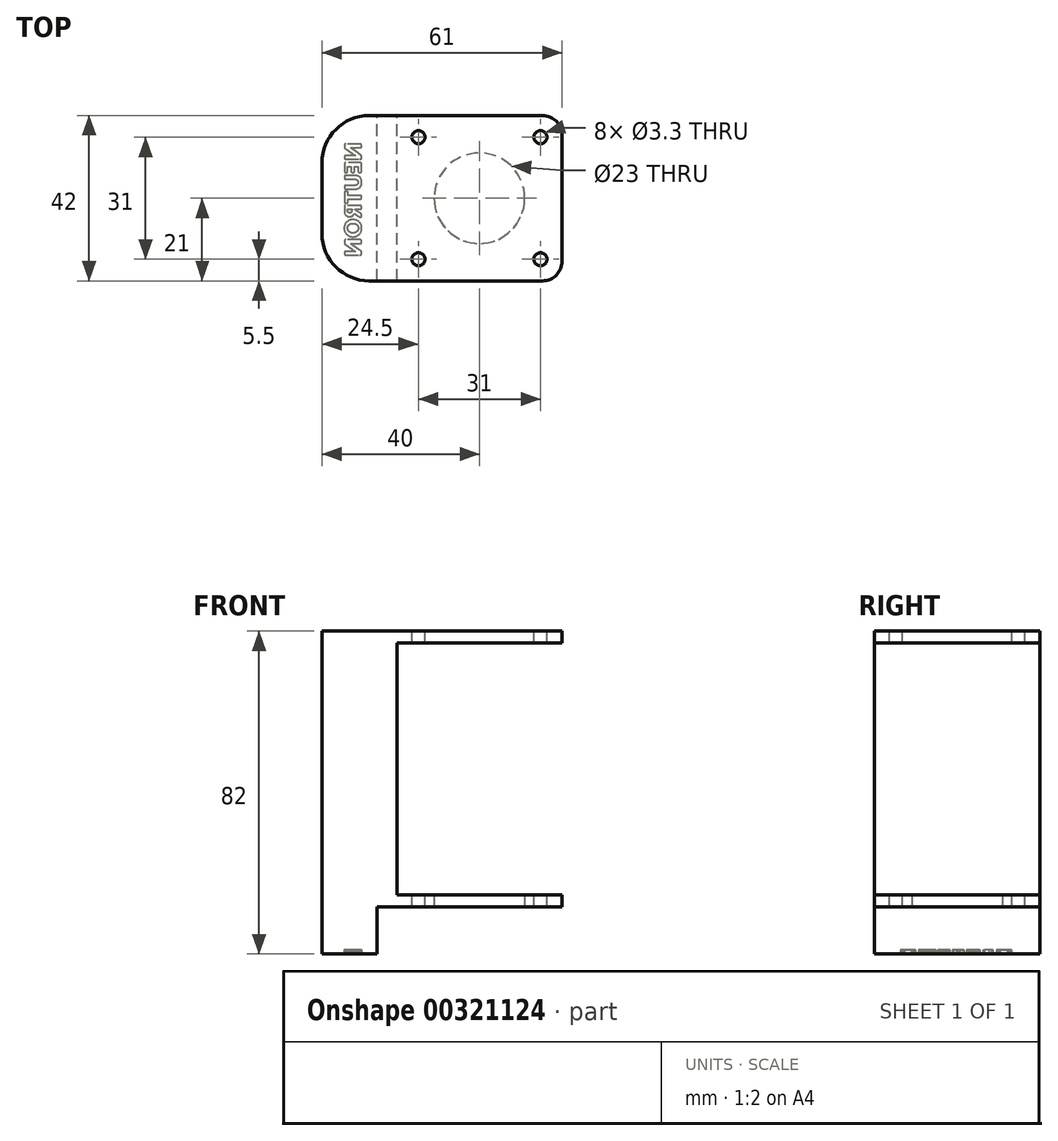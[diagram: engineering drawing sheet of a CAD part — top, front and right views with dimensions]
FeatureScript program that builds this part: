
annotation { "Feature Type Name" : "Feature", "Feature Type Description" : "" }
export const myFeature = defineFeature(function(context is Context, id is Id, definition is map)
    precondition{}
    {
        {
            var Q0;
            Q0=qCreatedBy(makeId("Top.planeOp"),FACE);
            var sketch = newSketch(context, id + "F0", { "sketchPlane" : qUnion([Q0])});
            skLineSegment(sketch, "E0.bottom", {"start": v(21, -21) * mm, "end": v(-21, -21) * mm});
            skLineSegment(sketch, "E0.top", {"start": v(21, 21) * mm, "end": v(-21, 21) * mm});
            skLineSegment(sketch, "E0.left", {"start": v(21, -21) * mm, "end": v(21, 21) * mm});
            skLineSegment(sketch, "E0.right", {"start": v(-21, -21) * mm, "end": v(-21, 21) * mm});
            skPoint(sketch, "E0.middle", {"position": v(0, 0) * mm});
            skSolve(sketch);
        }
        {
            var Q0;
            Q0=makeQuery(id+"F0.imprint","IMPRINT",FACE,{"disambiguationData":[TD([[makeQuery(id+"F0.imprint","IMPRINT",EDGE,{"derivedFrom":sQuery(id+"F0.wireOp",EDGE,"E0.bottom")}),-1.0]])]});
            extrude(context, id + "F1", {"entities" : qUnion([Q0]), "depth" : 3 * mm});
        }
        {
            var Q0;
            Q0=makeQuery(id+"F1.opExtrude","CAP_FACE",FACE,{"disambiguationData":[OSD([sQuery(id+"F0.wireOp",EDGE,"E0.bottom"),sQuery(id+"F0.wireOp",EDGE,"E0.top"),sQuery(id+"F0.wireOp",EDGE,"E0.left"),sQuery(id+"F0.wireOp",EDGE,"E0.right")])],"isStart":true});
            var sketch = newSketch(context, id + "F2", { "sketchPlane" : qUnion([Q0])});
            skLineSegment(sketch, "E1.bottom", {"start": v(-15.5, 15.5) * mm, "end": v(15.5, 15.5) * mm});
            skLineSegment(sketch, "E1.top", {"start": v(-15.5, -15.5) * mm, "end": v(15.5, -15.5) * mm});
            skLineSegment(sketch, "E1.left", {"start": v(-15.5, 15.5) * mm, "end": v(-15.5, -15.5) * mm});
            skLineSegment(sketch, "E1.right", {"start": v(15.5, 15.5) * mm, "end": v(15.5, -15.5) * mm});
            skPoint(sketch, "E1.middle", {"position": v(0, 0) * mm});
            skCircle(sketch, "E2", {"center": v(0, 0) * mm, "radius": 11.5 * mm});
            skSolve(sketch);
        }
        {
            var Q0;
            Q0=makeQuery(id+"F2.imprint","IMPRINT",FACE,{"disambiguationData":[TD([[makeQuery(id+"F2.imprint","IMPRINT",EDGE,{"derivedFrom":sQuery(id+"F2.wireOp",EDGE,"E2")}),1.0]])]});
            extrude(context, id + "F3", {"entities" : qUnion([Q0]), "operationType" : NewBodyOperationType.REMOVE, "oppositeDirection" : true, "depth" : 25 * mm});
        }
        {
            var Q0;
            Q0=makeQuery(id+"F1.opExtrude","SWEPT_FACE",FACE,{"disambiguationData":[OSD([sQuery(id+"F0.wireOp",EDGE,"E0.right")])]});
            var sketch = newSketch(context, id + "F4", { "sketchPlane" : qUnion([Q0])});
            skLineSegment(sketch, "E3.bottom", {"start": v(21, 0) * mm, "end": v(-21, 0) * mm});
            skLineSegment(sketch, "E3.top", {"start": v(21, 70) * mm, "end": v(-21, 70) * mm});
            skLineSegment(sketch, "E3.left", {"start": v(21, 0) * mm, "end": v(21, 70) * mm});
            skLineSegment(sketch, "E3.right", {"start": v(-21, 0) * mm, "end": v(-21, 70) * mm});
            skSolve(sketch);
        }
        {
            var Q0;
            {var subQ0=sQuery(id+"F4.wireOp",EDGE,"E3.bottom");Q0=makeQuery(id+"F4.imprint","IMPRINT",FACE,{"disambiguationData":[TD([[makeQuery(id+"F4.imprint","IMPRINT",EDGE,{"derivedFrom":subQ0}),-1.0]])]});}
            var Q1;
            {var subQ0=sQuery(id+"F4.wireOp",EDGE,"E3.top");Q1=makeQuery(id+"F4.imprint","IMPRINT",FACE,{"disambiguationData":[TD([[makeQuery(id+"F4.imprint","IMPRINT",EDGE,{"derivedFrom":subQ0}),1.0]])]});}
            extrude(context, id + "F5", {"entities" : qUnion([Q0, Q1]), "operationType" : NewBodyOperationType.ADD, "depth" : 19 * mm});
        }
        {
            var Q0;
            Q0=makeQuery(id+"F5.opExtrude","CAP_FACE",FACE,{"disambiguationData":[OSD([sQuery(id+"F4.wireOp",EDGE,"E3.bottom"),sQuery(id+"F4.wireOp",EDGE,"E3.top"),sQuery(id+"F4.wireOp",EDGE,"E3.left"),sQuery(id+"F4.wireOp",EDGE,"E3.right")])],"isStart":true});
            var sketch = newSketch(context, id + "F6", { "sketchPlane" : qUnion([Q0])});
            skLineSegment(sketch, "E4.bottom", {"start": v(21, 70) * mm, "end": v(-21, 70) * mm});
            skLineSegment(sketch, "E4.top", {"start": v(21, 67) * mm, "end": v(-21, 67) * mm});
            skLineSegment(sketch, "E4.left", {"start": v(21, 70) * mm, "end": v(21, 67) * mm});
            skLineSegment(sketch, "E4.right", {"start": v(-21, 70) * mm, "end": v(-21, 67) * mm});
            skSolve(sketch);
        }
        {
            var Q0;
            Q0 = qSketchRegion(id + "F6", true);
            extrude(context, id + "F7", {"entities" : qUnion([Q0]), "operationType" : NewBodyOperationType.ADD, "depth" : 42 * mm});
        }
        {
            var Q0;
            Q0=makeQuery(id+"F1.opExtrude","SWEPT_EDGE",EDGE,{"disambiguationData":[OSD([sQuery(id+"F0.wireOp",EDGE,"E0.top"),sQuery(id+"F0.wireOp",EDGE,"E0.left")])]});
            var Q1;
            Q1=makeQuery(id+"F1.opExtrude","SWEPT_EDGE",EDGE,{"disambiguationData":[OSD([sQuery(id+"F0.wireOp",EDGE,"E0.bottom"),sQuery(id+"F0.wireOp",EDGE,"E0.left")])]});
            var Q2;
            Q2=makeQuery(id+"F7.opExtrude","CAP_EDGE",EDGE,{"disambiguationData":[OSD([sQuery(id+"F6.wireOp",EDGE,"E4.right")])],"isStart":false});
            var Q3;
            Q3=makeQuery(id+"F7.opExtrude","CAP_EDGE",EDGE,{"disambiguationData":[OSD([sQuery(id+"F6.wireOp",EDGE,"E4.left")])],"isStart":false});
            fillet(context, id + "F8", {"entities" : qUnion([Q0, Q1, Q2, Q3]), "radius" : 5 * mm, "tangentPropagation" : true, "allowEdgeOverflow" : false});
        }
        {
            var Q0;
            Q0=sQuery(id+"F2.wireOp",VERTEX,"E1.left.end");
            var Q1;
            Q1=sQuery(id+"F2.wireOp",VERTEX,"E1.right.end");
            var Q2;
            Q2=sQuery(id+"F2.wireOp",VERTEX,"E1.right.start");
            var Q3;
            Q3=sQuery(id+"F2.wireOp",VERTEX,"E1.left.start");
            var Q4;
            Q4=makeQuery(id+"F1.opExtrude","SWEPT_BODY",BODY,{"disambiguationData":[OSD([sQuery(id+"F0.wireOp",EDGE,"E0.bottom"),sQuery(id+"F0.wireOp",EDGE,"E0.top"),sQuery(id+"F0.wireOp",EDGE,"E0.left"),sQuery(id+"F0.wireOp",EDGE,"E0.right")])]});
            hole(context, id + "F9", {"style" : HoleStyle.SIMPLE, "endStyle" : HoleEndStyle.THROUGH, "standardTappedOrClearance" : lookupTablePath({ "standard" : "ISO", "fit" : "Normal", "size" : "M3", "type" : "Clearance" }), "standardBlindInLast" : lookupTablePath({ "fit" : "Standard", "standard" : "ISO", "size" : "M3", "type" : "Clearance" }), "holeDiameter" : 3.3 * mm, "tappedDepth" : 12 * mm, "tapClearance" : 3, "locations" : qUnion([Q0, Q1, Q2, Q3]), "scope" : qUnion([Q4])});
        }
        {
            var Q0;
            Q0=makeQuery(id+"F5.opExtrude","CAP_EDGE",EDGE,{"disambiguationData":[OSD([sQuery(id+"F4.wireOp",EDGE,"E3.left")])],"isStart":false});
            var Q1;
            Q1=makeQuery(id+"F5.opExtrude","CAP_EDGE",EDGE,{"disambiguationData":[OSD([sQuery(id+"F4.wireOp",EDGE,"E3.right")])],"isStart":false});
            fillet(context, id + "F10", {"entities" : qUnion([Q0, Q1]), "radius" : 12 * mm, "tangentPropagation" : true, "allowEdgeOverflow" : false});
        }
        {
            var Q0;
            Q0=makeQuery(id+"F5.boolean.opBoolean","MERGE",FACE,{"derivedFrom":[makeQuery(id+"F1.opExtrude","CAP_FACE",FACE,{"disambiguationData":[OSD([sQuery(id+"F0.wireOp",EDGE,"E0.bottom"),sQuery(id+"F0.wireOp",EDGE,"E0.top"),sQuery(id+"F0.wireOp",EDGE,"E0.left"),sQuery(id+"F0.wireOp",EDGE,"E0.right")])],"isStart":true}),makeQuery(id+"F5.opExtrude","SWEPT_FACE",FACE,{"disambiguationData":[OSD([sQuery(id+"F4.wireOp",EDGE,"E3.bottom")])]})]});
            var sketch = newSketch(context, id + "F11", { "sketchPlane" : qUnion([Q0])});
            skLineSegment(sketch, "E5", {"start": v(-26, 21) * mm, "end": v(-26, -21) * mm});
            skSolve(sketch);
        }
        {
            var Q0;
            Q0 = qSketchRegion(id + "F11", true);
            var Q1;
            Q1=makeQuery(id+"F11.imprint","IMPRINT",FACE,{"disambiguationData":[TD([[makeQuery(id+"F11.imprint","IMPRINT",EDGE,{"derivedFrom":sQuery(id+"F11.wireOp",EDGE,"xwHfM6YB-dKn8-eSAS-4Oin-q8f2QlFwRjm7")}),1.0]])]});
            var Q2;
            {var subQ6=sQuery(id+"F11.wireOp",EDGE,"E5");Q2=makeQuery(id+"F11.imprint","IMPRINT",FACE,{"disambiguationData":[TD([[makeQuery(id+"F11.imprint","IMPRINT",EDGE,{"derivedFrom":subQ6}),-1.0]])]});}
            extrude(context, id + "F12", {"entities" : qUnion([Q0, Q1, Q2]), "operationType" : NewBodyOperationType.ADD, "depth" : 12 * mm});
        }
        {
            var Q0;
            Q0=makeQuery(id+"F12.opExtrude","CAP_FACE",FACE,{"disambiguationData":[OSD([sQuery(id+"F0.wireOp",EDGE,"E0.bottom"),sQuery(id+"F0.wireOp",EDGE,"E0.top"),sQuery(id+"F0.wireOp",EDGE,"E0.left"),sQuery(id+"F0.wireOp",EDGE,"E0.right"),sQuery(id+"F4.wireOp",EDGE,"E3.bottom"),sQuery(id+"F4.wireOp",EDGE,"E3.left"),sQuery(id+"F4.wireOp",EDGE,"E3.right"),sQuery(id+"F11.wireOp",EDGE,"xwHfM6YB-dKn8-eSAS-4Oin-q8f2QlFwRjm7")])],"isStart":false});
            var sketch = newSketch(context, id + "F13", { "sketchPlane" : qUnion([Q0])});
            skLineSegment(sketch, "E6", {"start": v(-34.33, -10.53) * mm, "end": v(-34.33, -10.5) * mm});
            skLineSegment(sketch, "E7", {"start": v(-34.33, -10.5) * mm, "end": v(-34.33, -10.44) * mm});
            skLineSegment(sketch, "E8", {"start": v(-34.33, -10.44) * mm, "end": v(-34.33, -10.36) * mm});
            skLineSegment(sketch, "E9", {"start": v(-34.33, -10.36) * mm, "end": v(-34.33, -10.28) * mm});
            skLineSegment(sketch, "E10", {"start": v(-34.33, -10.28) * mm, "end": v(-34.33, -10.23) * mm});
            skLineSegment(sketch, "E11", {"start": v(-34.33, -10.23) * mm, "end": v(-34.33, -10.18) * mm});
            skLineSegment(sketch, "E12", {"start": v(-34.33, -10.18) * mm, "end": v(-34.3, -10.1) * mm});
            skLineSegment(sketch, "E13", {"start": v(-34.3, -10.1) * mm, "end": v(-34.26, -10.02) * mm});
            skLineSegment(sketch, "E14", {"start": v(-34.26, -10.02) * mm, "end": v(-34.2, -9.97) * mm});
            skLineSegment(sketch, "E15", {"start": v(-34.2, -9.97) * mm, "end": v(-34.12, -9.93) * mm});
            skLineSegment(sketch, "E16", {"start": v(-34.12, -9.93) * mm, "end": v(-34.03, -9.91) * mm});
            skLineSegment(sketch, "E17", {"start": v(-34.03, -9.91) * mm, "end": v(-33.76, -9.91) * mm});
            skLineSegment(sketch, "E18", {"start": v(-33.76, -9.91) * mm, "end": v(-33.01, -9.91) * mm});
            skLineSegment(sketch, "E19", {"start": v(-33.01, -9.91) * mm, "end": v(-32.03, -9.91) * mm});
            skLineSegment(sketch, "E20", {"start": v(-32.03, -9.91) * mm, "end": v(-31.07, -9.91) * mm});
            skLineSegment(sketch, "E21", {"start": v(-31.07, -9.91) * mm, "end": v(-30.41, -9.91) * mm});
            skLineSegment(sketch, "E22", {"start": v(-30.41, -9.91) * mm, "end": v(-30.23, -9.91) * mm});
            skLineSegment(sketch, "E23", {"start": v(-30.23, -9.91) * mm, "end": v(-30.15, -9.93) * mm});
            skLineSegment(sketch, "E24", {"start": v(-30.15, -9.93) * mm, "end": v(-30.07, -9.98) * mm});
            skLineSegment(sketch, "E25", {"start": v(-30.07, -9.98) * mm, "end": v(-30.01, -10.04) * mm});
            skLineSegment(sketch, "E26", {"start": v(-30.01, -10.04) * mm, "end": v(-29.97, -10.11) * mm});
            skLineSegment(sketch, "E27", {"start": v(-29.97, -10.11) * mm, "end": v(-29.95, -10.2) * mm});
            skLineSegment(sketch, "E28", {"start": v(-29.95, -10.2) * mm, "end": v(-29.95, -10.25) * mm});
            skLineSegment(sketch, "E29", {"start": v(-29.95, -10.25) * mm, "end": v(-29.95, -10.33) * mm});
            skLineSegment(sketch, "E30", {"start": v(-29.95, -10.33) * mm, "end": v(-29.95, -10.45) * mm});
            skLineSegment(sketch, "E31", {"start": v(-29.95, -10.45) * mm, "end": v(-29.95, -10.56) * mm});
            skLineSegment(sketch, "E32", {"start": v(-29.95, -10.56) * mm, "end": v(-29.95, -10.65) * mm});
            skLineSegment(sketch, "E33", {"start": v(-29.95, -10.65) * mm, "end": v(-29.95, -10.68) * mm});
            skLineSegment(sketch, "E34", {"start": v(-29.95, -10.68) * mm, "end": v(-29.96, -10.74) * mm});
            skLineSegment(sketch, "E35", {"start": v(-29.96, -10.74) * mm, "end": v(-29.98, -10.79) * mm});
            skLineSegment(sketch, "E36", {"start": v(-29.98, -10.79) * mm, "end": v(-30, -10.83) * mm});
            skLineSegment(sketch, "E37", {"start": v(-30, -10.83) * mm, "end": v(-30.03, -10.88) * mm});
            skLineSegment(sketch, "E38", {"start": v(-30.03, -10.88) * mm, "end": v(-30.07, -10.91) * mm});
            skLineSegment(sketch, "E39", {"start": v(-30.07, -10.91) * mm, "end": v(-30.2, -11) * mm});
            skLineSegment(sketch, "E40", {"start": v(-30.2, -11) * mm, "end": v(-30.67, -11.34) * mm});
            skLineSegment(sketch, "E41", {"start": v(-30.67, -11.34) * mm, "end": v(-31.35, -11.82) * mm});
            skLineSegment(sketch, "E42", {"start": v(-31.35, -11.82) * mm, "end": v(-32.06, -12.32) * mm});
            skLineSegment(sketch, "E43", {"start": v(-32.06, -12.32) * mm, "end": v(-32.6, -12.7) * mm});
            skLineSegment(sketch, "E44", {"start": v(-32.6, -12.7) * mm, "end": v(-32.78, -12.83) * mm});
            skLineSegment(sketch, "E45", {"start": v(-32.78, -12.83) * mm, "end": v(-32.52, -12.83) * mm});
            skLineSegment(sketch, "E46", {"start": v(-32.52, -12.83) * mm, "end": v(-31.97, -12.83) * mm});
            skLineSegment(sketch, "E47", {"start": v(-31.97, -12.83) * mm, "end": v(-31.3, -12.83) * mm});
            skLineSegment(sketch, "E48", {"start": v(-31.3, -12.83) * mm, "end": v(-30.68, -12.83) * mm});
            skLineSegment(sketch, "E49", {"start": v(-30.68, -12.83) * mm, "end": v(-30.3, -12.83) * mm});
            skLineSegment(sketch, "E50", {"start": v(-30.3, -12.83) * mm, "end": v(-30.21, -12.84) * mm});
            skLineSegment(sketch, "E51", {"start": v(-30.21, -12.84) * mm, "end": v(-30.13, -12.86) * mm});
            skLineSegment(sketch, "E52", {"start": v(-30.13, -12.86) * mm, "end": v(-30.06, -12.9) * mm});
            skLineSegment(sketch, "E53", {"start": v(-30.06, -12.9) * mm, "end": v(-30, -12.97) * mm});
            skLineSegment(sketch, "E54", {"start": v(-30, -12.97) * mm, "end": v(-29.97, -13.05) * mm});
            skLineSegment(sketch, "E55", {"start": v(-29.97, -13.05) * mm, "end": v(-29.95, -13.14) * mm});
            skLineSegment(sketch, "E56", {"start": v(-29.95, -13.14) * mm, "end": v(-29.95, -13.17) * mm});
            skLineSegment(sketch, "E57", {"start": v(-29.95, -13.17) * mm, "end": v(-29.95, -13.24) * mm});
            skLineSegment(sketch, "E58", {"start": v(-29.95, -13.24) * mm, "end": v(-29.95, -13.32) * mm});
            skLineSegment(sketch, "E59", {"start": v(-29.95, -13.32) * mm, "end": v(-29.95, -13.4) * mm});
            skLineSegment(sketch, "E60", {"start": v(-29.95, -13.4) * mm, "end": v(-29.95, -13.46) * mm});
            skLineSegment(sketch, "E61", {"start": v(-29.95, -13.46) * mm, "end": v(-29.96, -13.5) * mm});
            skLineSegment(sketch, "E62", {"start": v(-29.96, -13.5) * mm, "end": v(-29.98, -13.6) * mm});
            skLineSegment(sketch, "E63", {"start": v(-29.98, -13.6) * mm, "end": v(-30.02, -13.66) * mm});
            skLineSegment(sketch, "E64", {"start": v(-30.02, -13.66) * mm, "end": v(-30.09, -13.72) * mm});
            skLineSegment(sketch, "E65", {"start": v(-30.09, -13.72) * mm, "end": v(-30.16, -13.76) * mm});
            skLineSegment(sketch, "E66", {"start": v(-30.16, -13.76) * mm, "end": v(-30.25, -13.78) * mm});
            skLineSegment(sketch, "E67", {"start": v(-30.25, -13.78) * mm, "end": v(-30.52, -13.78) * mm});
            skLineSegment(sketch, "E68", {"start": v(-30.52, -13.78) * mm, "end": v(-31.27, -13.78) * mm});
            skLineSegment(sketch, "E69", {"start": v(-31.27, -13.78) * mm, "end": v(-32.25, -13.78) * mm});
            skLineSegment(sketch, "E70", {"start": v(-32.25, -13.78) * mm, "end": v(-33.2, -13.78) * mm});
            skLineSegment(sketch, "E71", {"start": v(-33.2, -13.78) * mm, "end": v(-33.87, -13.78) * mm});
            skLineSegment(sketch, "E72", {"start": v(-33.87, -13.78) * mm, "end": v(-34.05, -13.77) * mm});
            skLineSegment(sketch, "E73", {"start": v(-34.05, -13.77) * mm, "end": v(-34.14, -13.75) * mm});
            skLineSegment(sketch, "E74", {"start": v(-34.14, -13.75) * mm, "end": v(-34.21, -13.71) * mm});
            skLineSegment(sketch, "E75", {"start": v(-34.21, -13.71) * mm, "end": v(-34.27, -13.65) * mm});
            skLineSegment(sketch, "E76", {"start": v(-34.27, -13.65) * mm, "end": v(-34.31, -13.57) * mm});
            skLineSegment(sketch, "E77", {"start": v(-34.31, -13.57) * mm, "end": v(-34.33, -13.49) * mm});
            skLineSegment(sketch, "E78", {"start": v(-34.33, -13.49) * mm, "end": v(-34.33, -13.44) * mm});
            skLineSegment(sketch, "E79", {"start": v(-34.33, -13.44) * mm, "end": v(-34.33, -13.35) * mm});
            skLineSegment(sketch, "E80", {"start": v(-34.33, -13.35) * mm, "end": v(-34.33, -13.23) * mm});
            skLineSegment(sketch, "E81", {"start": v(-34.33, -13.23) * mm, "end": v(-34.33, -13.11) * mm});
            skLineSegment(sketch, "E82", {"start": v(-34.33, -13.11) * mm, "end": v(-34.33, -13.03) * mm});
            skLineSegment(sketch, "E83", {"start": v(-34.33, -13.03) * mm, "end": v(-34.33, -12.99) * mm});
            skLineSegment(sketch, "E84", {"start": v(-34.33, -12.99) * mm, "end": v(-34.32, -12.94) * mm});
            skLineSegment(sketch, "E85", {"start": v(-34.32, -12.94) * mm, "end": v(-34.3, -12.89) * mm});
            skLineSegment(sketch, "E86", {"start": v(-34.3, -12.89) * mm, "end": v(-34.28, -12.84) * mm});
            skLineSegment(sketch, "E87", {"start": v(-34.28, -12.84) * mm, "end": v(-34.25, -12.8) * mm});
            skLineSegment(sketch, "E88", {"start": v(-34.25, -12.8) * mm, "end": v(-34.21, -12.76) * mm});
            skLineSegment(sketch, "E89", {"start": v(-34.21, -12.76) * mm, "end": v(-34.1, -12.67) * mm});
            skLineSegment(sketch, "E90", {"start": v(-34.1, -12.67) * mm, "end": v(-33.62, -12.34) * mm});
            skLineSegment(sketch, "E91", {"start": v(-33.62, -12.34) * mm, "end": v(-32.94, -11.85) * mm});
            skLineSegment(sketch, "E92", {"start": v(-32.94, -11.85) * mm, "end": v(-32.24, -11.35) * mm});
            skLineSegment(sketch, "E93", {"start": v(-32.24, -11.35) * mm, "end": v(-31.7, -10.97) * mm});
            skLineSegment(sketch, "E94", {"start": v(-31.7, -10.97) * mm, "end": v(-31.52, -10.84) * mm});
            skLineSegment(sketch, "E95", {"start": v(-31.52, -10.84) * mm, "end": v(-31.78, -10.84) * mm});
            skLineSegment(sketch, "E96", {"start": v(-31.78, -10.84) * mm, "end": v(-32.33, -10.84) * mm});
            skLineSegment(sketch, "E97", {"start": v(-32.33, -10.84) * mm, "end": v(-33, -10.84) * mm});
            skLineSegment(sketch, "E98", {"start": v(-33, -10.84) * mm, "end": v(-33.6, -10.84) * mm});
            skLineSegment(sketch, "E99", {"start": v(-33.6, -10.84) * mm, "end": v(-33.97, -10.84) * mm});
            skLineSegment(sketch, "E100", {"start": v(-33.97, -10.84) * mm, "end": v(-34.07, -10.83) * mm});
            skLineSegment(sketch, "E101", {"start": v(-34.07, -10.83) * mm, "end": v(-34.15, -10.8) * mm});
            skLineSegment(sketch, "E102", {"start": v(-34.15, -10.8) * mm, "end": v(-34.22, -10.76) * mm});
            skLineSegment(sketch, "E103", {"start": v(-34.22, -10.76) * mm, "end": v(-34.28, -10.7) * mm});
            skLineSegment(sketch, "E104", {"start": v(-34.28, -10.7) * mm, "end": v(-34.32, -10.62) * mm});
            skLineSegment(sketch, "E105", {"start": v(-34.32, -10.62) * mm, "end": v(-34.33, -10.53) * mm});
            skLineSegment(sketch, "E106", {"start": v(-34.33, -8.72) * mm, "end": v(-34.33, -8.52) * mm});
            skLineSegment(sketch, "E107", {"start": v(-34.33, -8.52) * mm, "end": v(-34.33, -8.07) * mm});
            skLineSegment(sketch, "E108", {"start": v(-34.33, -8.07) * mm, "end": v(-34.33, -7.52) * mm});
            skLineSegment(sketch, "E109", {"start": v(-34.33, -7.52) * mm, "end": v(-34.33, -7.06) * mm});
            skLineSegment(sketch, "E110", {"start": v(-34.33, -7.06) * mm, "end": v(-34.33, -6.87) * mm});
            skLineSegment(sketch, "E111", {"start": v(-34.33, -6.87) * mm, "end": v(-34.31, -6.77) * mm});
            skLineSegment(sketch, "E112", {"start": v(-34.31, -6.77) * mm, "end": v(-34.27, -6.69) * mm});
            skLineSegment(sketch, "E113", {"start": v(-34.27, -6.69) * mm, "end": v(-34.2, -6.62) * mm});
            skLineSegment(sketch, "E114", {"start": v(-34.2, -6.62) * mm, "end": v(-34.12, -6.58) * mm});
            skLineSegment(sketch, "E115", {"start": v(-34.12, -6.58) * mm, "end": v(-34.02, -6.56) * mm});
            skLineSegment(sketch, "E116", {"start": v(-34.02, -6.56) * mm, "end": v(-34, -6.56) * mm});
            skLineSegment(sketch, "E117", {"start": v(-34, -6.56) * mm, "end": v(-33.93, -6.56) * mm});
            skLineSegment(sketch, "E118", {"start": v(-33.93, -6.56) * mm, "end": v(-33.86, -6.56) * mm});
            skLineSegment(sketch, "E119", {"start": v(-33.86, -6.56) * mm, "end": v(-33.8, -6.56) * mm});
            skLineSegment(sketch, "E120", {"start": v(-33.8, -6.56) * mm, "end": v(-33.77, -6.56) * mm});
            skLineSegment(sketch, "E121", {"start": v(-33.77, -6.56) * mm, "end": v(-33.67, -6.58) * mm});
            skLineSegment(sketch, "E122", {"start": v(-33.67, -6.58) * mm, "end": v(-33.59, -6.62) * mm});
            skLineSegment(sketch, "E123", {"start": v(-33.59, -6.62) * mm, "end": v(-33.52, -6.69) * mm});
            skLineSegment(sketch, "E124", {"start": v(-33.52, -6.69) * mm, "end": v(-33.48, -6.77) * mm});
            skLineSegment(sketch, "E125", {"start": v(-33.48, -6.77) * mm, "end": v(-33.46, -6.87) * mm});
            skLineSegment(sketch, "E126", {"start": v(-33.46, -6.87) * mm, "end": v(-33.46, -7) * mm});
            skLineSegment(sketch, "E127", {"start": v(-33.46, -7) * mm, "end": v(-33.46, -7.3) * mm});
            skLineSegment(sketch, "E128", {"start": v(-33.46, -7.3) * mm, "end": v(-33.46, -7.66) * mm});
            skLineSegment(sketch, "E129", {"start": v(-33.46, -7.66) * mm, "end": v(-33.46, -7.96) * mm});
            skLineSegment(sketch, "E130", {"start": v(-33.46, -7.96) * mm, "end": v(-33.46, -8.08) * mm});
            skLineSegment(sketch, "E131", {"start": v(-33.46, -8.08) * mm, "end": v(-33.37, -8.08) * mm});
            skLineSegment(sketch, "E132", {"start": v(-33.37, -8.08) * mm, "end": v(-33.15, -8.08) * mm});
            skLineSegment(sketch, "E133", {"start": v(-33.15, -8.08) * mm, "end": v(-32.9, -8.08) * mm});
            skLineSegment(sketch, "E134", {"start": v(-32.9, -8.08) * mm, "end": v(-32.67, -8.08) * mm});
            skLineSegment(sketch, "E135", {"start": v(-32.67, -8.08) * mm, "end": v(-32.58, -8.08) * mm});
            skLineSegment(sketch, "E136", {"start": v(-32.58, -8.08) * mm, "end": v(-32.58, -7.96) * mm});
            skLineSegment(sketch, "E137", {"start": v(-32.58, -7.96) * mm, "end": v(-32.58, -7.66) * mm});
            skLineSegment(sketch, "E138", {"start": v(-32.58, -7.66) * mm, "end": v(-32.58, -7.3) * mm});
            skLineSegment(sketch, "E139", {"start": v(-32.58, -7.3) * mm, "end": v(-32.58, -7) * mm});
            skLineSegment(sketch, "E140", {"start": v(-32.58, -7) * mm, "end": v(-32.58, -6.87) * mm});
            skLineSegment(sketch, "E141", {"start": v(-32.58, -6.87) * mm, "end": v(-32.56, -6.77) * mm});
            skLineSegment(sketch, "E142", {"start": v(-32.56, -6.77) * mm, "end": v(-32.52, -6.69) * mm});
            skLineSegment(sketch, "E143", {"start": v(-32.52, -6.69) * mm, "end": v(-32.45, -6.62) * mm});
            skLineSegment(sketch, "E144", {"start": v(-32.45, -6.62) * mm, "end": v(-32.37, -6.58) * mm});
            skLineSegment(sketch, "E145", {"start": v(-32.37, -6.58) * mm, "end": v(-32.27, -6.56) * mm});
            skLineSegment(sketch, "E146", {"start": v(-32.27, -6.56) * mm, "end": v(-32.25, -6.56) * mm});
            skLineSegment(sketch, "E147", {"start": v(-32.25, -6.56) * mm, "end": v(-32.19, -6.56) * mm});
            skLineSegment(sketch, "E148", {"start": v(-32.19, -6.56) * mm, "end": v(-32.12, -6.56) * mm});
            skLineSegment(sketch, "E149", {"start": v(-32.12, -6.56) * mm, "end": v(-32.06, -6.56) * mm});
            skLineSegment(sketch, "E150", {"start": v(-32.06, -6.56) * mm, "end": v(-32.04, -6.56) * mm});
            skLineSegment(sketch, "E151", {"start": v(-32.04, -6.56) * mm, "end": v(-31.94, -6.58) * mm});
            skLineSegment(sketch, "E152", {"start": v(-31.94, -6.58) * mm, "end": v(-31.85, -6.62) * mm});
            skLineSegment(sketch, "E153", {"start": v(-31.85, -6.62) * mm, "end": v(-31.79, -6.69) * mm});
            skLineSegment(sketch, "E154", {"start": v(-31.79, -6.69) * mm, "end": v(-31.74, -6.77) * mm});
            skLineSegment(sketch, "E155", {"start": v(-31.74, -6.77) * mm, "end": v(-31.73, -6.87) * mm});
            skLineSegment(sketch, "E156", {"start": v(-31.73, -6.87) * mm, "end": v(-31.73, -7) * mm});
            skLineSegment(sketch, "E157", {"start": v(-31.73, -7) * mm, "end": v(-31.73, -7.3) * mm});
            skLineSegment(sketch, "E158", {"start": v(-31.73, -7.3) * mm, "end": v(-31.73, -7.66) * mm});
            skLineSegment(sketch, "E159", {"start": v(-31.73, -7.66) * mm, "end": v(-31.73, -7.96) * mm});
            skLineSegment(sketch, "E160", {"start": v(-31.73, -7.96) * mm, "end": v(-31.73, -8.08) * mm});
            skLineSegment(sketch, "E161", {"start": v(-31.73, -8.08) * mm, "end": v(-31.63, -8.08) * mm});
            skLineSegment(sketch, "E162", {"start": v(-31.63, -8.08) * mm, "end": v(-31.4, -8.08) * mm});
            skLineSegment(sketch, "E163", {"start": v(-31.4, -8.08) * mm, "end": v(-31.14, -8.08) * mm});
            skLineSegment(sketch, "E164", {"start": v(-31.14, -8.08) * mm, "end": v(-30.91, -8.08) * mm});
            skLineSegment(sketch, "E165", {"start": v(-30.91, -8.08) * mm, "end": v(-30.82, -8.08) * mm});
            skLineSegment(sketch, "E166", {"start": v(-30.82, -8.08) * mm, "end": v(-30.82, -7.96) * mm});
            skLineSegment(sketch, "E167", {"start": v(-30.82, -7.96) * mm, "end": v(-30.82, -7.66) * mm});
            skLineSegment(sketch, "E168", {"start": v(-30.82, -7.66) * mm, "end": v(-30.82, -7.3) * mm});
            skLineSegment(sketch, "E169", {"start": v(-30.82, -7.3) * mm, "end": v(-30.82, -7) * mm});
            skLineSegment(sketch, "E170", {"start": v(-30.82, -7) * mm, "end": v(-30.82, -6.87) * mm});
            skLineSegment(sketch, "E171", {"start": v(-30.82, -6.87) * mm, "end": v(-30.8, -6.77) * mm});
            skLineSegment(sketch, "E172", {"start": v(-30.8, -6.77) * mm, "end": v(-30.76, -6.69) * mm});
            skLineSegment(sketch, "E173", {"start": v(-30.76, -6.69) * mm, "end": v(-30.7, -6.62) * mm});
            skLineSegment(sketch, "E174", {"start": v(-30.7, -6.62) * mm, "end": v(-30.6, -6.58) * mm});
            skLineSegment(sketch, "E175", {"start": v(-30.6, -6.58) * mm, "end": v(-30.51, -6.56) * mm});
            skLineSegment(sketch, "E176", {"start": v(-30.51, -6.56) * mm, "end": v(-30.48, -6.56) * mm});
            skLineSegment(sketch, "E177", {"start": v(-30.48, -6.56) * mm, "end": v(-30.42, -6.56) * mm});
            skLineSegment(sketch, "E178", {"start": v(-30.42, -6.56) * mm, "end": v(-30.35, -6.56) * mm});
            skLineSegment(sketch, "E179", {"start": v(-30.35, -6.56) * mm, "end": v(-30.29, -6.56) * mm});
            skLineSegment(sketch, "E180", {"start": v(-30.29, -6.56) * mm, "end": v(-30.26, -6.56) * mm});
            skLineSegment(sketch, "E181", {"start": v(-30.26, -6.56) * mm, "end": v(-30.16, -6.58) * mm});
            skLineSegment(sketch, "E182", {"start": v(-30.16, -6.58) * mm, "end": v(-30.08, -6.62) * mm});
            skLineSegment(sketch, "E183", {"start": v(-30.08, -6.62) * mm, "end": v(-30.01, -6.69) * mm});
            skLineSegment(sketch, "E184", {"start": v(-30.01, -6.69) * mm, "end": v(-29.97, -6.77) * mm});
            skLineSegment(sketch, "E185", {"start": v(-29.97, -6.77) * mm, "end": v(-29.95, -6.87) * mm});
            skLineSegment(sketch, "E186", {"start": v(-29.95, -6.87) * mm, "end": v(-29.95, -7.06) * mm});
            skLineSegment(sketch, "E187", {"start": v(-29.95, -7.06) * mm, "end": v(-29.95, -7.52) * mm});
            skLineSegment(sketch, "E188", {"start": v(-29.95, -7.52) * mm, "end": v(-29.95, -8.07) * mm});
            skLineSegment(sketch, "E189", {"start": v(-29.95, -8.07) * mm, "end": v(-29.95, -8.52) * mm});
            skLineSegment(sketch, "E190", {"start": v(-29.95, -8.52) * mm, "end": v(-29.95, -8.72) * mm});
            skLineSegment(sketch, "E191", {"start": v(-29.95, -8.72) * mm, "end": v(-29.97, -8.81) * mm});
            skLineSegment(sketch, "E192", {"start": v(-29.97, -8.81) * mm, "end": v(-30.01, -8.9) * mm});
            skLineSegment(sketch, "E193", {"start": v(-30.01, -8.9) * mm, "end": v(-30.08, -8.97) * mm});
            skLineSegment(sketch, "E194", {"start": v(-30.08, -8.97) * mm, "end": v(-30.16, -9.01) * mm});
            skLineSegment(sketch, "E195", {"start": v(-30.16, -9.01) * mm, "end": v(-30.26, -9.03) * mm});
            skLineSegment(sketch, "E196", {"start": v(-30.26, -9.03) * mm, "end": v(-30.65, -9.03) * mm});
            skLineSegment(sketch, "E197", {"start": v(-30.65, -9.03) * mm, "end": v(-31.58, -9.03) * mm});
            skLineSegment(sketch, "E198", {"start": v(-31.58, -9.03) * mm, "end": v(-32.7, -9.03) * mm});
            skLineSegment(sketch, "E199", {"start": v(-32.7, -9.03) * mm, "end": v(-33.63, -9.03) * mm});
            skLineSegment(sketch, "E200", {"start": v(-33.63, -9.03) * mm, "end": v(-34.02, -9.03) * mm});
            skLineSegment(sketch, "E201", {"start": v(-34.02, -9.03) * mm, "end": v(-34.12, -9.01) * mm});
            skLineSegment(sketch, "E202", {"start": v(-34.12, -9.01) * mm, "end": v(-34.2, -8.97) * mm});
            skLineSegment(sketch, "E203", {"start": v(-34.2, -8.97) * mm, "end": v(-34.27, -8.9) * mm});
            skLineSegment(sketch, "E204", {"start": v(-34.27, -8.9) * mm, "end": v(-34.31, -8.81) * mm});
            skLineSegment(sketch, "E205", {"start": v(-34.31, -8.81) * mm, "end": v(-34.33, -8.72) * mm});
            skLineSegment(sketch, "E206", {"start": v(-34.33, -5.45) * mm, "end": v(-34.33, -5.42) * mm});
            skLineSegment(sketch, "E207", {"start": v(-34.33, -5.42) * mm, "end": v(-34.33, -5.35) * mm});
            skLineSegment(sketch, "E208", {"start": v(-34.33, -5.35) * mm, "end": v(-34.33, -5.27) * mm});
            skLineSegment(sketch, "E209", {"start": v(-34.33, -5.27) * mm, "end": v(-34.33, -5.19) * mm});
            skLineSegment(sketch, "E210", {"start": v(-34.33, -5.19) * mm, "end": v(-34.33, -5.14) * mm});
            skLineSegment(sketch, "E211", {"start": v(-34.33, -5.14) * mm, "end": v(-34.32, -5.07) * mm});
            skLineSegment(sketch, "E212", {"start": v(-34.32, -5.07) * mm, "end": v(-34.29, -4.99) * mm});
            skLineSegment(sketch, "E213", {"start": v(-34.29, -4.99) * mm, "end": v(-34.23, -4.92) * mm});
            skLineSegment(sketch, "E214", {"start": v(-34.23, -4.92) * mm, "end": v(-34.16, -4.87) * mm});
            skLineSegment(sketch, "E215", {"start": v(-34.16, -4.87) * mm, "end": v(-34.07, -4.84) * mm});
            skLineSegment(sketch, "E216", {"start": v(-34.07, -4.84) * mm, "end": v(-33.97, -4.83) * mm});
            skLineSegment(sketch, "E217", {"start": v(-33.97, -4.83) * mm, "end": v(-33.57, -4.83) * mm});
            skLineSegment(sketch, "E218", {"start": v(-33.57, -4.83) * mm, "end": v(-32.94, -4.83) * mm});
            skLineSegment(sketch, "E219", {"start": v(-32.94, -4.83) * mm, "end": v(-32.29, -4.83) * mm});
            skLineSegment(sketch, "E220", {"start": v(-32.29, -4.83) * mm, "end": v(-31.8, -4.83) * mm});
            skLineSegment(sketch, "E221", {"start": v(-31.8, -4.83) * mm, "end": v(-31.62, -4.83) * mm});
            skLineSegment(sketch, "E222", {"start": v(-31.62, -4.83) * mm, "end": v(-31.49, -4.82) * mm});
            skLineSegment(sketch, "E223", {"start": v(-31.49, -4.82) * mm, "end": v(-31.37, -4.8) * mm});
            skLineSegment(sketch, "E224", {"start": v(-31.37, -4.8) * mm, "end": v(-31.25, -4.76) * mm});
            skLineSegment(sketch, "E225", {"start": v(-31.25, -4.76) * mm, "end": v(-31.15, -4.7) * mm});
            skLineSegment(sketch, "E226", {"start": v(-31.15, -4.7) * mm, "end": v(-31.06, -4.63) * mm});
            skLineSegment(sketch, "E227", {"start": v(-31.06, -4.63) * mm, "end": v(-30.98, -4.55) * mm});
            skLineSegment(sketch, "E228", {"start": v(-30.98, -4.55) * mm, "end": v(-30.92, -4.46) * mm});
            skLineSegment(sketch, "E229", {"start": v(-30.92, -4.46) * mm, "end": v(-30.87, -4.35) * mm});
            skLineSegment(sketch, "E230", {"start": v(-30.87, -4.35) * mm, "end": v(-30.84, -4.24) * mm});
            skLineSegment(sketch, "E231", {"start": v(-30.84, -4.24) * mm, "end": v(-30.83, -4.12) * mm});
            skLineSegment(sketch, "E232", {"start": v(-30.83, -4.12) * mm, "end": v(-30.83, -3.99) * mm});
            skLineSegment(sketch, "E233", {"start": v(-30.83, -3.99) * mm, "end": v(-30.85, -3.85) * mm});
            skLineSegment(sketch, "E234", {"start": v(-30.85, -3.85) * mm, "end": v(-30.89, -3.73) * mm});
            skLineSegment(sketch, "E235", {"start": v(-30.89, -3.73) * mm, "end": v(-30.94, -3.63) * mm});
            skLineSegment(sketch, "E236", {"start": v(-30.94, -3.63) * mm, "end": v(-31, -3.53) * mm});
            skLineSegment(sketch, "E237", {"start": v(-31, -3.53) * mm, "end": v(-31.1, -3.45) * mm});
            skLineSegment(sketch, "E238", {"start": v(-31.1, -3.45) * mm, "end": v(-31.2, -3.38) * mm});
            skLineSegment(sketch, "E239", {"start": v(-31.2, -3.38) * mm, "end": v(-31.3, -3.33) * mm});
            skLineSegment(sketch, "E240", {"start": v(-31.3, -3.33) * mm, "end": v(-31.43, -3.3) * mm});
            skLineSegment(sketch, "E241", {"start": v(-31.43, -3.3) * mm, "end": v(-31.57, -3.28) * mm});
            skLineSegment(sketch, "E242", {"start": v(-31.57, -3.28) * mm, "end": v(-31.7, -3.27) * mm});
            skLineSegment(sketch, "E243", {"start": v(-31.7, -3.27) * mm, "end": v(-31.99, -3.27) * mm});
            skLineSegment(sketch, "E244", {"start": v(-31.99, -3.27) * mm, "end": v(-32.55, -3.27) * mm});
            skLineSegment(sketch, "E245", {"start": v(-32.55, -3.27) * mm, "end": v(-33.2, -3.27) * mm});
            skLineSegment(sketch, "E246", {"start": v(-33.2, -3.27) * mm, "end": v(-33.76, -3.27) * mm});
            skLineSegment(sketch, "E247", {"start": v(-33.76, -3.27) * mm, "end": v(-34.02, -3.27) * mm});
            skLineSegment(sketch, "E248", {"start": v(-34.02, -3.27) * mm, "end": v(-34.1, -3.26) * mm});
            skLineSegment(sketch, "E249", {"start": v(-34.1, -3.26) * mm, "end": v(-34.19, -3.22) * mm});
            skLineSegment(sketch, "E250", {"start": v(-34.19, -3.22) * mm, "end": v(-34.25, -3.16) * mm});
            skLineSegment(sketch, "E251", {"start": v(-34.25, -3.16) * mm, "end": v(-34.3, -3.09) * mm});
            skLineSegment(sketch, "E252", {"start": v(-34.3, -3.09) * mm, "end": v(-34.33, -3) * mm});
            skLineSegment(sketch, "E253", {"start": v(-34.33, -3) * mm, "end": v(-34.33, -2.95) * mm});
            skLineSegment(sketch, "E254", {"start": v(-34.33, -2.95) * mm, "end": v(-34.33, -2.9) * mm});
            skLineSegment(sketch, "E255", {"start": v(-34.33, -2.9) * mm, "end": v(-34.33, -2.8) * mm});
            skLineSegment(sketch, "E256", {"start": v(-34.33, -2.8) * mm, "end": v(-34.33, -2.72) * mm});
            skLineSegment(sketch, "E257", {"start": v(-34.33, -2.72) * mm, "end": v(-34.33, -2.66) * mm});
            skLineSegment(sketch, "E258", {"start": v(-34.33, -2.66) * mm, "end": v(-34.33, -2.62) * mm});
            skLineSegment(sketch, "E259", {"start": v(-34.33, -2.62) * mm, "end": v(-34.3, -2.53) * mm});
            skLineSegment(sketch, "E260", {"start": v(-34.3, -2.53) * mm, "end": v(-34.25, -2.45) * mm});
            skLineSegment(sketch, "E261", {"start": v(-34.25, -2.45) * mm, "end": v(-34.19, -2.4) * mm});
            skLineSegment(sketch, "E262", {"start": v(-34.19, -2.4) * mm, "end": v(-34.1, -2.35) * mm});
            skLineSegment(sketch, "E263", {"start": v(-34.1, -2.35) * mm, "end": v(-34.02, -2.34) * mm});
            skLineSegment(sketch, "E264", {"start": v(-34.02, -2.34) * mm, "end": v(-33.73, -2.34) * mm});
            skLineSegment(sketch, "E265", {"start": v(-33.73, -2.34) * mm, "end": v(-33.13, -2.34) * mm});
            skLineSegment(sketch, "E266", {"start": v(-33.13, -2.34) * mm, "end": v(-32.42, -2.34) * mm});
            skLineSegment(sketch, "E267", {"start": v(-32.42, -2.34) * mm, "end": v(-31.8, -2.34) * mm});
            skLineSegment(sketch, "E268", {"start": v(-31.8, -2.34) * mm, "end": v(-31.5, -2.34) * mm});
            skLineSegment(sketch, "E269", {"start": v(-31.5, -2.34) * mm, "end": v(-31.38, -2.35) * mm});
            skLineSegment(sketch, "E270", {"start": v(-31.38, -2.35) * mm, "end": v(-31.23, -2.37) * mm});
            skLineSegment(sketch, "E271", {"start": v(-31.23, -2.37) * mm, "end": v(-31.08, -2.4) * mm});
            skLineSegment(sketch, "E272", {"start": v(-31.08, -2.4) * mm, "end": v(-30.94, -2.45) * mm});
            skLineSegment(sketch, "E273", {"start": v(-30.94, -2.45) * mm, "end": v(-30.79, -2.5) * mm});
            skLineSegment(sketch, "E274", {"start": v(-30.79, -2.5) * mm, "end": v(-30.64, -2.58) * mm});
            skLineSegment(sketch, "E275", {"start": v(-30.64, -2.58) * mm, "end": v(-30.5, -2.67) * mm});
            skLineSegment(sketch, "E276", {"start": v(-30.5, -2.67) * mm, "end": v(-30.37, -2.78) * mm});
            skLineSegment(sketch, "E277", {"start": v(-30.37, -2.78) * mm, "end": v(-30.26, -2.9) * mm});
            skLineSegment(sketch, "E278", {"start": v(-30.26, -2.9) * mm, "end": v(-30.17, -3.03) * mm});
            skLineSegment(sketch, "E279", {"start": v(-30.17, -3.03) * mm, "end": v(-30.08, -3.18) * mm});
            skLineSegment(sketch, "E280", {"start": v(-30.08, -3.18) * mm, "end": v(-30.01, -3.34) * mm});
            skLineSegment(sketch, "E281", {"start": v(-30.01, -3.34) * mm, "end": v(-29.96, -3.5) * mm});
            skLineSegment(sketch, "E282", {"start": v(-29.96, -3.5) * mm, "end": v(-29.92, -3.68) * mm});
            skLineSegment(sketch, "E283", {"start": v(-29.92, -3.68) * mm, "end": v(-29.9, -3.85) * mm});
            skLineSegment(sketch, "E284", {"start": v(-29.9, -3.85) * mm, "end": v(-29.9, -4.05) * mm});
            skLineSegment(sketch, "E285", {"start": v(-29.9, -4.05) * mm, "end": v(-29.91, -4.37) * mm});
            skLineSegment(sketch, "E286", {"start": v(-29.91, -4.37) * mm, "end": v(-29.97, -4.66) * mm});
            skLineSegment(sketch, "E287", {"start": v(-29.97, -4.66) * mm, "end": v(-30.06, -4.91) * mm});
            skLineSegment(sketch, "E288", {"start": v(-30.06, -4.91) * mm, "end": v(-30.2, -5.13) * mm});
            skLineSegment(sketch, "E289", {"start": v(-30.2, -5.13) * mm, "end": v(-30.36, -5.31) * mm});
            skLineSegment(sketch, "E290", {"start": v(-30.36, -5.31) * mm, "end": v(-30.55, -5.46) * mm});
            skLineSegment(sketch, "E291", {"start": v(-30.55, -5.46) * mm, "end": v(-30.74, -5.58) * mm});
            skLineSegment(sketch, "E292", {"start": v(-30.74, -5.58) * mm, "end": v(-30.94, -5.67) * mm});
            skLineSegment(sketch, "E293", {"start": v(-30.94, -5.67) * mm, "end": v(-31.14, -5.73) * mm});
            skLineSegment(sketch, "E294", {"start": v(-31.14, -5.73) * mm, "end": v(-31.35, -5.76) * mm});
            skLineSegment(sketch, "E295", {"start": v(-31.35, -5.76) * mm, "end": v(-31.52, -5.76) * mm});
            skLineSegment(sketch, "E296", {"start": v(-31.52, -5.76) * mm, "end": v(-31.97, -5.76) * mm});
            skLineSegment(sketch, "E297", {"start": v(-31.97, -5.76) * mm, "end": v(-32.66, -5.76) * mm});
            skLineSegment(sketch, "E298", {"start": v(-32.66, -5.76) * mm, "end": v(-33.37, -5.76) * mm});
            skLineSegment(sketch, "E299", {"start": v(-33.37, -5.76) * mm, "end": v(-33.88, -5.76) * mm});
            skLineSegment(sketch, "E300", {"start": v(-33.88, -5.76) * mm, "end": v(-34.05, -5.76) * mm});
            skLineSegment(sketch, "E301", {"start": v(-34.05, -5.76) * mm, "end": v(-34.14, -5.74) * mm});
            skLineSegment(sketch, "E302", {"start": v(-34.14, -5.74) * mm, "end": v(-34.21, -5.7) * mm});
            skLineSegment(sketch, "E303", {"start": v(-34.21, -5.7) * mm, "end": v(-34.28, -5.63) * mm});
            skLineSegment(sketch, "E304", {"start": v(-34.28, -5.63) * mm, "end": v(-34.31, -5.55) * mm});
            skLineSegment(sketch, "E305", {"start": v(-34.31, -5.55) * mm, "end": v(-34.33, -5.45) * mm});
            skLineSegment(sketch, "E306", {"start": v(-34.33, -1.42) * mm, "end": v(-34.33, -1.3) * mm});
            skLineSegment(sketch, "E307", {"start": v(-34.33, -1.3) * mm, "end": v(-34.33, -0.98) * mm});
            skLineSegment(sketch, "E308", {"start": v(-34.33, -0.98) * mm, "end": v(-34.33, -0.54) * mm});
            skLineSegment(sketch, "E309", {"start": v(-34.33, -0.54) * mm, "end": v(-34.33, -0.05) * mm});
            skLineSegment(sketch, "E310", {"start": v(-34.33, -0.05) * mm, "end": v(-34.33, 0.4) * mm});
            skLineSegment(sketch, "E311", {"start": v(-34.33, 0.4) * mm, "end": v(-34.33, 0.74) * mm});
            skLineSegment(sketch, "E312", {"start": v(-34.33, 0.74) * mm, "end": v(-34.33, 0.9) * mm});
            skLineSegment(sketch, "E313", {"start": v(-34.33, 0.9) * mm, "end": v(-34.32, 0.96) * mm});
            skLineSegment(sketch, "E314", {"start": v(-34.32, 0.96) * mm, "end": v(-34.3, 1.03) * mm});
            skLineSegment(sketch, "E315", {"start": v(-34.3, 1.03) * mm, "end": v(-34.27, 1.09) * mm});
            skLineSegment(sketch, "E316", {"start": v(-34.27, 1.09) * mm, "end": v(-34.22, 1.14) * mm});
            skLineSegment(sketch, "E317", {"start": v(-34.22, 1.14) * mm, "end": v(-34.17, 1.17) * mm});
            skLineSegment(sketch, "E318", {"start": v(-34.17, 1.17) * mm, "end": v(-34.1, 1.2) * mm});
            skLineSegment(sketch, "E319", {"start": v(-34.1, 1.2) * mm, "end": v(-34.04, 1.21) * mm});
            skLineSegment(sketch, "E320", {"start": v(-34.04, 1.21) * mm, "end": v(-34.01, 1.21) * mm});
            skLineSegment(sketch, "E321", {"start": v(-34.01, 1.21) * mm, "end": v(-33.97, 1.21) * mm});
            skLineSegment(sketch, "E322", {"start": v(-33.97, 1.21) * mm, "end": v(-33.92, 1.21) * mm});
            skLineSegment(sketch, "E323", {"start": v(-33.92, 1.21) * mm, "end": v(-33.85, 1.21) * mm});
            skLineSegment(sketch, "E324", {"start": v(-33.85, 1.21) * mm, "end": v(-33.8, 1.21) * mm});
            skLineSegment(sketch, "E325", {"start": v(-33.8, 1.21) * mm, "end": v(-33.74, 1.21) * mm});
            skLineSegment(sketch, "E326", {"start": v(-33.74, 1.21) * mm, "end": v(-33.71, 1.21) * mm});
            skLineSegment(sketch, "E327", {"start": v(-33.71, 1.21) * mm, "end": v(-33.67, 1.21) * mm});
            skLineSegment(sketch, "E328", {"start": v(-33.67, 1.21) * mm, "end": v(-33.6, 1.2) * mm});
            skLineSegment(sketch, "E329", {"start": v(-33.6, 1.2) * mm, "end": v(-33.54, 1.16) * mm});
            skLineSegment(sketch, "E330", {"start": v(-33.54, 1.16) * mm, "end": v(-33.49, 1.12) * mm});
            skLineSegment(sketch, "E331", {"start": v(-33.49, 1.12) * mm, "end": v(-33.45, 1.07) * mm});
            skLineSegment(sketch, "E332", {"start": v(-33.45, 1.07) * mm, "end": v(-33.42, 1.01) * mm});
            skLineSegment(sketch, "E333", {"start": v(-33.42, 1.01) * mm, "end": v(-33.4, 0.94) * mm});
            skLineSegment(sketch, "E334", {"start": v(-33.4, 0.94) * mm, "end": v(-33.4, 0.9) * mm});
            skLineSegment(sketch, "E335", {"start": v(-33.4, 0.9) * mm, "end": v(-33.4, 0.83) * mm});
            skLineSegment(sketch, "E336", {"start": v(-33.4, 0.83) * mm, "end": v(-33.4, 0.72) * mm});
            skLineSegment(sketch, "E337", {"start": v(-33.4, 0.72) * mm, "end": v(-33.4, 0.58) * mm});
            skLineSegment(sketch, "E338", {"start": v(-33.4, 0.58) * mm, "end": v(-33.4, 0.43) * mm});
            skLineSegment(sketch, "E339", {"start": v(-33.4, 0.43) * mm, "end": v(-33.4, 0.31) * mm});
            skLineSegment(sketch, "E340", {"start": v(-33.4, 0.31) * mm, "end": v(-33.4, 0.23) * mm});
            skLineSegment(sketch, "E341", {"start": v(-33.4, 0.23) * mm, "end": v(-33.38, 0.2) * mm});
            skLineSegment(sketch, "E342", {"start": v(-33.38, 0.2) * mm, "end": v(-33.13, 0.2) * mm});
            skLineSegment(sketch, "E343", {"start": v(-33.13, 0.2) * mm, "end": v(-32.64, 0.2) * mm});
            skLineSegment(sketch, "E344", {"start": v(-32.64, 0.2) * mm, "end": v(-32.02, 0.2) * mm});
            skLineSegment(sketch, "E345", {"start": v(-32.02, 0.2) * mm, "end": v(-31.37, 0.2) * mm});
            skLineSegment(sketch, "E346", {"start": v(-31.37, 0.2) * mm, "end": v(-30.79, 0.2) * mm});
            skLineSegment(sketch, "E347", {"start": v(-30.79, 0.2) * mm, "end": v(-30.39, 0.2) * mm});
            skLineSegment(sketch, "E348", {"start": v(-30.39, 0.2) * mm, "end": v(-30.25, 0.2) * mm});
            skLineSegment(sketch, "E349", {"start": v(-30.25, 0.2) * mm, "end": v(-30.18, 0.2) * mm});
            skLineSegment(sketch, "E350", {"start": v(-30.18, 0.2) * mm, "end": v(-30.12, 0.18) * mm});
            skLineSegment(sketch, "E351", {"start": v(-30.12, 0.18) * mm, "end": v(-30.06, 0.14) * mm});
            skLineSegment(sketch, "E352", {"start": v(-30.06, 0.14) * mm, "end": v(-30.02, 0.1) * mm});
            skLineSegment(sketch, "E353", {"start": v(-30.02, 0.1) * mm, "end": v(-29.98, 0.03) * mm});
            skLineSegment(sketch, "E354", {"start": v(-29.98, 0.03) * mm, "end": v(-29.96, -0.03) * mm});
            skLineSegment(sketch, "E355", {"start": v(-29.96, -0.03) * mm, "end": v(-29.95, -0.1) * mm});
            skLineSegment(sketch, "E356", {"start": v(-29.95, -0.1) * mm, "end": v(-29.95, -0.16) * mm});
            skLineSegment(sketch, "E357", {"start": v(-29.95, -0.16) * mm, "end": v(-29.95, -0.22) * mm});
            skLineSegment(sketch, "E358", {"start": v(-29.95, -0.22) * mm, "end": v(-29.95, -0.3) * mm});
            skLineSegment(sketch, "E359", {"start": v(-29.95, -0.3) * mm, "end": v(-29.95, -0.35) * mm});
            skLineSegment(sketch, "E360", {"start": v(-29.95, -0.35) * mm, "end": v(-29.95, -0.4) * mm});
            skLineSegment(sketch, "E361", {"start": v(-29.95, -0.4) * mm, "end": v(-29.95, -0.42) * mm});
            skLineSegment(sketch, "E362", {"start": v(-29.95, -0.42) * mm, "end": v(-29.96, -0.48) * mm});
            skLineSegment(sketch, "E363", {"start": v(-29.96, -0.48) * mm, "end": v(-29.98, -0.55) * mm});
            skLineSegment(sketch, "E364", {"start": v(-29.98, -0.55) * mm, "end": v(-30.01, -0.6) * mm});
            skLineSegment(sketch, "E365", {"start": v(-30.01, -0.6) * mm, "end": v(-30.06, -0.66) * mm});
            skLineSegment(sketch, "E366", {"start": v(-30.06, -0.66) * mm, "end": v(-30.11, -0.7) * mm});
            skLineSegment(sketch, "E367", {"start": v(-30.11, -0.7) * mm, "end": v(-30.17, -0.72) * mm});
            skLineSegment(sketch, "E368", {"start": v(-30.17, -0.72) * mm, "end": v(-30.24, -0.73) * mm});
            skLineSegment(sketch, "E369", {"start": v(-30.24, -0.73) * mm, "end": v(-30.35, -0.73) * mm});
            skLineSegment(sketch, "E370", {"start": v(-30.35, -0.73) * mm, "end": v(-30.72, -0.73) * mm});
            skLineSegment(sketch, "E371", {"start": v(-30.72, -0.73) * mm, "end": v(-31.28, -0.73) * mm});
            skLineSegment(sketch, "E372", {"start": v(-31.28, -0.73) * mm, "end": v(-31.92, -0.73) * mm});
            skLineSegment(sketch, "E373", {"start": v(-31.92, -0.73) * mm, "end": v(-32.56, -0.73) * mm});
            skLineSegment(sketch, "E374", {"start": v(-32.56, -0.73) * mm, "end": v(-33.07, -0.73) * mm});
            skLineSegment(sketch, "E375", {"start": v(-33.07, -0.73) * mm, "end": v(-33.37, -0.73) * mm});
            skLineSegment(sketch, "E376", {"start": v(-33.37, -0.73) * mm, "end": v(-33.4, -0.75) * mm});
            skLineSegment(sketch, "E377", {"start": v(-33.4, -0.75) * mm, "end": v(-33.4, -0.82) * mm});
            skLineSegment(sketch, "E378", {"start": v(-33.4, -0.82) * mm, "end": v(-33.4, -0.94) * mm});
            skLineSegment(sketch, "E379", {"start": v(-33.4, -0.94) * mm, "end": v(-33.4, -1.08) * mm});
            skLineSegment(sketch, "E380", {"start": v(-33.4, -1.08) * mm, "end": v(-33.4, -1.22) * mm});
            skLineSegment(sketch, "E381", {"start": v(-33.4, -1.22) * mm, "end": v(-33.4, -1.34) * mm});
            skLineSegment(sketch, "E382", {"start": v(-33.4, -1.34) * mm, "end": v(-33.4, -1.4) * mm});
            skLineSegment(sketch, "E383", {"start": v(-33.4, -1.4) * mm, "end": v(-33.4, -1.45) * mm});
            skLineSegment(sketch, "E384", {"start": v(-33.4, -1.45) * mm, "end": v(-33.42, -1.52) * mm});
            skLineSegment(sketch, "E385", {"start": v(-33.42, -1.52) * mm, "end": v(-33.44, -1.58) * mm});
            skLineSegment(sketch, "E386", {"start": v(-33.44, -1.58) * mm, "end": v(-33.48, -1.63) * mm});
            skLineSegment(sketch, "E387", {"start": v(-33.48, -1.63) * mm, "end": v(-33.53, -1.68) * mm});
            skLineSegment(sketch, "E388", {"start": v(-33.53, -1.68) * mm, "end": v(-33.6, -1.7) * mm});
            skLineSegment(sketch, "E389", {"start": v(-33.6, -1.7) * mm, "end": v(-33.66, -1.73) * mm});
            skLineSegment(sketch, "E390", {"start": v(-33.66, -1.73) * mm, "end": v(-33.7, -1.73) * mm});
            skLineSegment(sketch, "E391", {"start": v(-33.7, -1.73) * mm, "end": v(-33.74, -1.73) * mm});
            skLineSegment(sketch, "E392", {"start": v(-33.74, -1.73) * mm, "end": v(-33.78, -1.73) * mm});
            skLineSegment(sketch, "E393", {"start": v(-33.78, -1.73) * mm, "end": v(-33.85, -1.73) * mm});
            skLineSegment(sketch, "E394", {"start": v(-33.85, -1.73) * mm, "end": v(-33.91, -1.73) * mm});
            skLineSegment(sketch, "E395", {"start": v(-33.91, -1.73) * mm, "end": v(-33.97, -1.73) * mm});
            skLineSegment(sketch, "E396", {"start": v(-33.97, -1.73) * mm, "end": v(-34, -1.73) * mm});
            skLineSegment(sketch, "E397", {"start": v(-34, -1.73) * mm, "end": v(-34.03, -1.73) * mm});
            skLineSegment(sketch, "E398", {"start": v(-34.03, -1.73) * mm, "end": v(-34.1, -1.72) * mm});
            skLineSegment(sketch, "E399", {"start": v(-34.1, -1.72) * mm, "end": v(-34.16, -1.7) * mm});
            skLineSegment(sketch, "E400", {"start": v(-34.16, -1.7) * mm, "end": v(-34.22, -1.66) * mm});
            skLineSegment(sketch, "E401", {"start": v(-34.22, -1.66) * mm, "end": v(-34.26, -1.61) * mm});
            skLineSegment(sketch, "E402", {"start": v(-34.26, -1.61) * mm, "end": v(-34.3, -1.55) * mm});
            skLineSegment(sketch, "E403", {"start": v(-34.3, -1.55) * mm, "end": v(-34.32, -1.5) * mm});
            skLineSegment(sketch, "E404", {"start": v(-34.32, -1.5) * mm, "end": v(-34.33, -1.42) * mm});
            skLineSegment(sketch, "E405", {"start": v(-34.02, 1.83) * mm, "end": v(-34.1, 1.84) * mm});
            skLineSegment(sketch, "E406", {"start": v(-34.1, 1.84) * mm, "end": v(-34.18, 1.87) * mm});
            skLineSegment(sketch, "E407", {"start": v(-34.18, 1.87) * mm, "end": v(-34.24, 1.92) * mm});
            skLineSegment(sketch, "E408", {"start": v(-34.24, 1.92) * mm, "end": v(-34.3, 1.99) * mm});
            skLineSegment(sketch, "E409", {"start": v(-34.3, 1.99) * mm, "end": v(-34.32, 2.06) * mm});
            skLineSegment(sketch, "E410", {"start": v(-34.32, 2.06) * mm, "end": v(-34.33, 2.14) * mm});
            skLineSegment(sketch, "E411", {"start": v(-34.33, 2.14) * mm, "end": v(-34.33, 2.25) * mm});
            skLineSegment(sketch, "E412", {"start": v(-34.33, 2.25) * mm, "end": v(-34.33, 2.47) * mm});
            skLineSegment(sketch, "E413", {"start": v(-34.33, 2.47) * mm, "end": v(-34.33, 2.76) * mm});
            skLineSegment(sketch, "E414", {"start": v(-34.33, 2.76) * mm, "end": v(-34.33, 3.03) * mm});
            skLineSegment(sketch, "E415", {"start": v(-34.33, 3.03) * mm, "end": v(-34.33, 3.22) * mm});
            skLineSegment(sketch, "E416", {"start": v(-34.33, 3.22) * mm, "end": v(-34.33, 3.32) * mm});
            skLineSegment(sketch, "E417", {"start": v(-34.33, 3.32) * mm, "end": v(-34.31, 3.54) * mm});
            skLineSegment(sketch, "E418", {"start": v(-34.31, 3.54) * mm, "end": v(-34.28, 3.73) * mm});
            skLineSegment(sketch, "E419", {"start": v(-34.28, 3.73) * mm, "end": v(-34.22, 3.91) * mm});
            skLineSegment(sketch, "E420", {"start": v(-34.22, 3.91) * mm, "end": v(-34.15, 4.08) * mm});
            skLineSegment(sketch, "E421", {"start": v(-34.15, 4.08) * mm, "end": v(-34.05, 4.22) * mm});
            skLineSegment(sketch, "E422", {"start": v(-34.05, 4.22) * mm, "end": v(-33.94, 4.36) * mm});
            skLineSegment(sketch, "E423", {"start": v(-33.94, 4.36) * mm, "end": v(-33.81, 4.47) * mm});
            skLineSegment(sketch, "E424", {"start": v(-33.81, 4.47) * mm, "end": v(-33.67, 4.56) * mm});
            skLineSegment(sketch, "E425", {"start": v(-33.67, 4.56) * mm, "end": v(-33.5, 4.62) * mm});
            skLineSegment(sketch, "E426", {"start": v(-33.5, 4.62) * mm, "end": v(-33.34, 4.67) * mm});
            skLineSegment(sketch, "E427", {"start": v(-33.34, 4.67) * mm, "end": v(-33.15, 4.69) * mm});
            skLineSegment(sketch, "E428", {"start": v(-33.15, 4.69) * mm, "end": v(-33, 4.7) * mm});
            skLineSegment(sketch, "E429", {"start": v(-33, 4.7) * mm, "end": v(-32.88, 4.68) * mm});
            skLineSegment(sketch, "E430", {"start": v(-32.88, 4.68) * mm, "end": v(-32.76, 4.66) * mm});
            skLineSegment(sketch, "E431", {"start": v(-32.76, 4.66) * mm, "end": v(-32.64, 4.63) * mm});
            skLineSegment(sketch, "E432", {"start": v(-32.64, 4.63) * mm, "end": v(-32.52, 4.6) * mm});
            skLineSegment(sketch, "E433", {"start": v(-32.52, 4.6) * mm, "end": v(-32.4, 4.54) * mm});
            skLineSegment(sketch, "E434", {"start": v(-32.4, 4.54) * mm, "end": v(-32.28, 4.48) * mm});
            skLineSegment(sketch, "E435", {"start": v(-32.28, 4.48) * mm, "end": v(-32.16, 4.4) * mm});
            skLineSegment(sketch, "E436", {"start": v(-32.16, 4.4) * mm, "end": v(-32.06, 4.3) * mm});
            skLineSegment(sketch, "E437", {"start": v(-32.06, 4.3) * mm, "end": v(-31.96, 4.2) * mm});
            skLineSegment(sketch, "E438", {"start": v(-31.96, 4.2) * mm, "end": v(-31.88, 4.06) * mm});
            skLineSegment(sketch, "E439", {"start": v(-31.88, 4.06) * mm, "end": v(-31.8, 3.92) * mm});
            skLineSegment(sketch, "E440", {"start": v(-31.8, 3.92) * mm, "end": v(-31.72, 3.9) * mm});
            skLineSegment(sketch, "E441", {"start": v(-31.72, 3.9) * mm, "end": v(-31.5, 4.05) * mm});
            skLineSegment(sketch, "E442", {"start": v(-31.5, 4.05) * mm, "end": v(-31.19, 4.27) * mm});
            skLineSegment(sketch, "E443", {"start": v(-31.19, 4.27) * mm, "end": v(-30.85, 4.5) * mm});
            skLineSegment(sketch, "E444", {"start": v(-30.85, 4.5) * mm, "end": v(-30.57, 4.68) * mm});
            skLineSegment(sketch, "E445", {"start": v(-30.57, 4.68) * mm, "end": v(-30.44, 4.77) * mm});
            skLineSegment(sketch, "E446", {"start": v(-30.44, 4.77) * mm, "end": v(-30.35, 4.81) * mm});
            skLineSegment(sketch, "E447", {"start": v(-30.35, 4.81) * mm, "end": v(-30.23, 4.82) * mm});
            skLineSegment(sketch, "E448", {"start": v(-30.23, 4.82) * mm, "end": v(-30.13, 4.8) * mm});
            skLineSegment(sketch, "E449", {"start": v(-30.13, 4.8) * mm, "end": v(-30.04, 4.73) * mm});
            skLineSegment(sketch, "E450", {"start": v(-30.04, 4.73) * mm, "end": v(-29.98, 4.64) * mm});
            skLineSegment(sketch, "E451", {"start": v(-29.98, 4.64) * mm, "end": v(-29.95, 4.52) * mm});
            skLineSegment(sketch, "E452", {"start": v(-29.95, 4.52) * mm, "end": v(-29.95, 4.5) * mm});
            skLineSegment(sketch, "E453", {"start": v(-29.95, 4.5) * mm, "end": v(-29.95, 4.43) * mm});
            skLineSegment(sketch, "E454", {"start": v(-29.95, 4.43) * mm, "end": v(-29.95, 4.35) * mm});
            skLineSegment(sketch, "E455", {"start": v(-29.95, 4.35) * mm, "end": v(-29.95, 4.26) * mm});
            skLineSegment(sketch, "E456", {"start": v(-29.95, 4.26) * mm, "end": v(-29.95, 4.2) * mm});
            skLineSegment(sketch, "E457", {"start": v(-29.95, 4.2) * mm, "end": v(-29.95, 4.17) * mm});
            skLineSegment(sketch, "E458", {"start": v(-29.95, 4.17) * mm, "end": v(-29.96, 4.12) * mm});
            skLineSegment(sketch, "E459", {"start": v(-29.96, 4.12) * mm, "end": v(-29.97, 4.07) * mm});
            skLineSegment(sketch, "E460", {"start": v(-29.97, 4.07) * mm, "end": v(-30, 4.03) * mm});
            skLineSegment(sketch, "E461", {"start": v(-30, 4.03) * mm, "end": v(-30.02, 3.98) * mm});
            skLineSegment(sketch, "E462", {"start": v(-30.02, 3.98) * mm, "end": v(-30.06, 3.95) * mm});
            skLineSegment(sketch, "E463", {"start": v(-30.06, 3.95) * mm, "end": v(-30.1, 3.92) * mm});
            skLineSegment(sketch, "E464", {"start": v(-30.1, 3.92) * mm, "end": v(-30.25, 3.81) * mm});
            skLineSegment(sketch, "E465", {"start": v(-30.25, 3.81) * mm, "end": v(-30.57, 3.6) * mm});
            skLineSegment(sketch, "E466", {"start": v(-30.57, 3.6) * mm, "end": v(-30.96, 3.34) * mm});
            skLineSegment(sketch, "E467", {"start": v(-30.96, 3.34) * mm, "end": v(-31.33, 3.1) * mm});
            skLineSegment(sketch, "E468", {"start": v(-31.33, 3.1) * mm, "end": v(-31.58, 2.92) * mm});
            skLineSegment(sketch, "E469", {"start": v(-31.58, 2.92) * mm, "end": v(-31.65, 2.88) * mm});
            skLineSegment(sketch, "E470", {"start": v(-31.65, 2.88) * mm, "end": v(-31.65, 2.84) * mm});
            skLineSegment(sketch, "E471", {"start": v(-31.65, 2.84) * mm, "end": v(-31.65, 2.82) * mm});
            skLineSegment(sketch, "E472", {"start": v(-31.65, 2.82) * mm, "end": v(-31.65, 2.8) * mm});
            skLineSegment(sketch, "E473", {"start": v(-31.65, 2.8) * mm, "end": v(-31.63, 2.77) * mm});
            skLineSegment(sketch, "E474", {"start": v(-31.63, 2.77) * mm, "end": v(-31.45, 2.77) * mm});
            skLineSegment(sketch, "E475", {"start": v(-31.45, 2.77) * mm, "end": v(-31.14, 2.77) * mm});
            skLineSegment(sketch, "E476", {"start": v(-31.14, 2.77) * mm, "end": v(-30.79, 2.77) * mm});
            skLineSegment(sketch, "E477", {"start": v(-30.79, 2.77) * mm, "end": v(-30.48, 2.77) * mm});
            skLineSegment(sketch, "E478", {"start": v(-30.48, 2.77) * mm, "end": v(-30.29, 2.77) * mm});
            skLineSegment(sketch, "E479", {"start": v(-30.29, 2.77) * mm, "end": v(-30.22, 2.77) * mm});
            skLineSegment(sketch, "E480", {"start": v(-30.22, 2.77) * mm, "end": v(-30.14, 2.75) * mm});
            skLineSegment(sketch, "E481", {"start": v(-30.14, 2.75) * mm, "end": v(-30.07, 2.7) * mm});
            skLineSegment(sketch, "E482", {"start": v(-30.07, 2.7) * mm, "end": v(-30.01, 2.65) * mm});
            skLineSegment(sketch, "E483", {"start": v(-30.01, 2.65) * mm, "end": v(-29.97, 2.58) * mm});
            skLineSegment(sketch, "E484", {"start": v(-29.97, 2.58) * mm, "end": v(-29.95, 2.5) * mm});
            skLineSegment(sketch, "E485", {"start": v(-29.95, 2.5) * mm, "end": v(-29.95, 2.45) * mm});
            skLineSegment(sketch, "E486", {"start": v(-29.95, 2.45) * mm, "end": v(-29.95, 2.4) * mm});
            skLineSegment(sketch, "E487", {"start": v(-29.95, 2.4) * mm, "end": v(-29.95, 2.33) * mm});
            skLineSegment(sketch, "E488", {"start": v(-29.95, 2.33) * mm, "end": v(-29.95, 2.24) * mm});
            skLineSegment(sketch, "E489", {"start": v(-29.95, 2.24) * mm, "end": v(-29.95, 2.18) * mm});
            skLineSegment(sketch, "E490", {"start": v(-29.95, 2.18) * mm, "end": v(-29.95, 2.14) * mm});
            skLineSegment(sketch, "E491", {"start": v(-29.95, 2.14) * mm, "end": v(-29.96, 2.07) * mm});
            skLineSegment(sketch, "E492", {"start": v(-29.96, 2.07) * mm, "end": v(-29.99, 2) * mm});
            skLineSegment(sketch, "E493", {"start": v(-29.99, 2) * mm, "end": v(-30.03, 1.93) * mm});
            skLineSegment(sketch, "E494", {"start": v(-30.03, 1.93) * mm, "end": v(-30.1, 1.88) * mm});
            skLineSegment(sketch, "E495", {"start": v(-30.1, 1.88) * mm, "end": v(-30.17, 1.84) * mm});
            skLineSegment(sketch, "E496", {"start": v(-30.17, 1.84) * mm, "end": v(-30.25, 1.83) * mm});
            skLineSegment(sketch, "E497", {"start": v(-30.25, 1.83) * mm, "end": v(-30.5, 1.83) * mm});
            skLineSegment(sketch, "E498", {"start": v(-30.5, 1.83) * mm, "end": v(-31.17, 1.83) * mm});
            skLineSegment(sketch, "E499", {"start": v(-31.17, 1.83) * mm, "end": v(-32.08, 1.83) * mm});
            skLineSegment(sketch, "E500", {"start": v(-32.08, 1.83) * mm, "end": v(-33.01, 1.83) * mm});
            skLineSegment(sketch, "E501", {"start": v(-33.01, 1.83) * mm, "end": v(-33.73, 1.83) * mm});
            skLineSegment(sketch, "E502", {"start": v(-33.73, 1.83) * mm, "end": v(-34.02, 1.83) * mm});
            skLineSegment(sketch, "E503", {"start": v(-33.55, 2.78) * mm, "end": v(-33.5, 2.78) * mm});
            skLineSegment(sketch, "E504", {"start": v(-33.5, 2.78) * mm, "end": v(-33.38, 2.78) * mm});
            skLineSegment(sketch, "E505", {"start": v(-33.38, 2.78) * mm, "end": v(-33.2, 2.78) * mm});
            skLineSegment(sketch, "E506", {"start": v(-33.2, 2.78) * mm, "end": v(-33, 2.78) * mm});
            skLineSegment(sketch, "E507", {"start": v(-33, 2.78) * mm, "end": v(-32.8, 2.78) * mm});
            skLineSegment(sketch, "E508", {"start": v(-32.8, 2.78) * mm, "end": v(-32.6, 2.78) * mm});
            skLineSegment(sketch, "E509", {"start": v(-32.6, 2.78) * mm, "end": v(-32.47, 2.78) * mm});
            skLineSegment(sketch, "E510", {"start": v(-32.47, 2.78) * mm, "end": v(-32.41, 2.78) * mm});
            skLineSegment(sketch, "E511", {"start": v(-32.41, 2.78) * mm, "end": v(-32.4, 2.8) * mm});
            skLineSegment(sketch, "E512", {"start": v(-32.4, 2.8) * mm, "end": v(-32.4, 2.84) * mm});
            skLineSegment(sketch, "E513", {"start": v(-32.4, 2.84) * mm, "end": v(-32.4, 2.87) * mm});
            skLineSegment(sketch, "E514", {"start": v(-32.4, 2.87) * mm, "end": v(-32.4, 2.9) * mm});
            skLineSegment(sketch, "E515", {"start": v(-32.4, 2.9) * mm, "end": v(-32.4, 2.94) * mm});
            skLineSegment(sketch, "E516", {"start": v(-32.4, 2.94) * mm, "end": v(-32.4, 2.97) * mm});
            skLineSegment(sketch, "E517", {"start": v(-32.4, 2.97) * mm, "end": v(-32.41, 3.1) * mm});
            skLineSegment(sketch, "E518", {"start": v(-32.41, 3.1) * mm, "end": v(-32.43, 3.25) * mm});
            skLineSegment(sketch, "E519", {"start": v(-32.43, 3.25) * mm, "end": v(-32.47, 3.39) * mm});
            skLineSegment(sketch, "E520", {"start": v(-32.47, 3.39) * mm, "end": v(-32.53, 3.5) * mm});
            skLineSegment(sketch, "E521", {"start": v(-32.53, 3.5) * mm, "end": v(-32.6, 3.59) * mm});
            skLineSegment(sketch, "E522", {"start": v(-32.6, 3.59) * mm, "end": v(-32.7, 3.65) * mm});
            skLineSegment(sketch, "E523", {"start": v(-32.7, 3.65) * mm, "end": v(-32.81, 3.7) * mm});
            skLineSegment(sketch, "E524", {"start": v(-32.81, 3.7) * mm, "end": v(-32.94, 3.72) * mm});
            skLineSegment(sketch, "E525", {"start": v(-32.94, 3.72) * mm, "end": v(-33.04, 3.72) * mm});
            skLineSegment(sketch, "E526", {"start": v(-33.04, 3.72) * mm, "end": v(-33.1, 3.72) * mm});
            skLineSegment(sketch, "E527", {"start": v(-33.1, 3.72) * mm, "end": v(-33.15, 3.7) * mm});
            skLineSegment(sketch, "E528", {"start": v(-33.15, 3.7) * mm, "end": v(-33.2, 3.69) * mm});
            skLineSegment(sketch, "E529", {"start": v(-33.2, 3.69) * mm, "end": v(-33.25, 3.66) * mm});
            skLineSegment(sketch, "E530", {"start": v(-33.25, 3.66) * mm, "end": v(-33.3, 3.64) * mm});
            skLineSegment(sketch, "E531", {"start": v(-33.3, 3.64) * mm, "end": v(-33.34, 3.6) * mm});
            skLineSegment(sketch, "E532", {"start": v(-33.34, 3.6) * mm, "end": v(-33.38, 3.56) * mm});
            skLineSegment(sketch, "E533", {"start": v(-33.38, 3.56) * mm, "end": v(-33.42, 3.51) * mm});
            skLineSegment(sketch, "E534", {"start": v(-33.42, 3.51) * mm, "end": v(-33.45, 3.46) * mm});
            skLineSegment(sketch, "E535", {"start": v(-33.45, 3.46) * mm, "end": v(-33.48, 3.4) * mm});
            skLineSegment(sketch, "E536", {"start": v(-33.48, 3.4) * mm, "end": v(-33.5, 3.35) * mm});
            skLineSegment(sketch, "E537", {"start": v(-33.5, 3.35) * mm, "end": v(-33.52, 3.28) * mm});
            skLineSegment(sketch, "E538", {"start": v(-33.52, 3.28) * mm, "end": v(-33.53, 3.22) * mm});
            skLineSegment(sketch, "E539", {"start": v(-33.53, 3.22) * mm, "end": v(-33.54, 3.14) * mm});
            skLineSegment(sketch, "E540", {"start": v(-33.54, 3.14) * mm, "end": v(-33.55, 3.07) * mm});
            skLineSegment(sketch, "E541", {"start": v(-33.55, 3.07) * mm, "end": v(-33.55, 3) * mm});
            skLineSegment(sketch, "E542", {"start": v(-33.55, 3) * mm, "end": v(-33.55, 2.96) * mm});
            skLineSegment(sketch, "E543", {"start": v(-33.55, 2.96) * mm, "end": v(-33.55, 2.92) * mm});
            skLineSegment(sketch, "E544", {"start": v(-33.55, 2.92) * mm, "end": v(-33.55, 2.88) * mm});
            skLineSegment(sketch, "E545", {"start": v(-33.55, 2.88) * mm, "end": v(-33.55, 2.85) * mm});
            skLineSegment(sketch, "E546", {"start": v(-33.55, 2.85) * mm, "end": v(-33.55, 2.81) * mm});
            skLineSegment(sketch, "E547", {"start": v(-33.55, 2.81) * mm, "end": v(-33.55, 2.78) * mm});
            skLineSegment(sketch, "E548", {"start": v(-32.14, 5.4) * mm, "end": v(-32.38, 5.41) * mm});
            skLineSegment(sketch, "E549", {"start": v(-32.38, 5.41) * mm, "end": v(-32.6, 5.44) * mm});
            skLineSegment(sketch, "E550", {"start": v(-32.6, 5.44) * mm, "end": v(-32.81, 5.5) * mm});
            skLineSegment(sketch, "E551", {"start": v(-32.81, 5.5) * mm, "end": v(-33.02, 5.56) * mm});
            skLineSegment(sketch, "E552", {"start": v(-33.02, 5.56) * mm, "end": v(-33.2, 5.65) * mm});
            skLineSegment(sketch, "E553", {"start": v(-33.2, 5.65) * mm, "end": v(-33.4, 5.75) * mm});
            skLineSegment(sketch, "E554", {"start": v(-33.4, 5.75) * mm, "end": v(-33.56, 5.88) * mm});
            skLineSegment(sketch, "E555", {"start": v(-33.56, 5.88) * mm, "end": v(-33.72, 6.02) * mm});
            skLineSegment(sketch, "E556", {"start": v(-33.72, 6.02) * mm, "end": v(-33.87, 6.19) * mm});
            skLineSegment(sketch, "E557", {"start": v(-33.87, 6.19) * mm, "end": v(-34, 6.35) * mm});
            skLineSegment(sketch, "E558", {"start": v(-34, 6.35) * mm, "end": v(-34.11, 6.53) * mm});
            skLineSegment(sketch, "E559", {"start": v(-34.11, 6.53) * mm, "end": v(-34.2, 6.71) * mm});
            skLineSegment(sketch, "E560", {"start": v(-34.2, 6.71) * mm, "end": v(-34.27, 6.9) * mm});
            skLineSegment(sketch, "E561", {"start": v(-34.27, 6.9) * mm, "end": v(-34.33, 7.1) * mm});
            skLineSegment(sketch, "E562", {"start": v(-34.33, 7.1) * mm, "end": v(-34.36, 7.3) * mm});
            skLineSegment(sketch, "E563", {"start": v(-34.36, 7.3) * mm, "end": v(-34.38, 7.51) * mm});
            skLineSegment(sketch, "E564", {"start": v(-34.38, 7.51) * mm, "end": v(-34.37, 7.74) * mm});
            skLineSegment(sketch, "E565", {"start": v(-34.37, 7.74) * mm, "end": v(-34.35, 7.97) * mm});
            skLineSegment(sketch, "E566", {"start": v(-34.35, 7.97) * mm, "end": v(-34.3, 8.19) * mm});
            skLineSegment(sketch, "E567", {"start": v(-34.3, 8.19) * mm, "end": v(-34.24, 8.4) * mm});
            skLineSegment(sketch, "E568", {"start": v(-34.24, 8.4) * mm, "end": v(-34.16, 8.59) * mm});
            skLineSegment(sketch, "E569", {"start": v(-34.16, 8.59) * mm, "end": v(-34.06, 8.77) * mm});
            skLineSegment(sketch, "E570", {"start": v(-34.06, 8.77) * mm, "end": v(-33.94, 8.95) * mm});
            skLineSegment(sketch, "E571", {"start": v(-33.94, 8.95) * mm, "end": v(-33.8, 9.12) * mm});
            skLineSegment(sketch, "E572", {"start": v(-33.8, 9.12) * mm, "end": v(-33.64, 9.27) * mm});
            skLineSegment(sketch, "E573", {"start": v(-33.64, 9.27) * mm, "end": v(-33.47, 9.4) * mm});
            skLineSegment(sketch, "E574", {"start": v(-33.47, 9.4) * mm, "end": v(-33.3, 9.52) * mm});
            skLineSegment(sketch, "E575", {"start": v(-33.3, 9.52) * mm, "end": v(-33.1, 9.62) * mm});
            skLineSegment(sketch, "E576", {"start": v(-33.1, 9.62) * mm, "end": v(-32.9, 9.7) * mm});
            skLineSegment(sketch, "E577", {"start": v(-32.9, 9.7) * mm, "end": v(-32.7, 9.75) * mm});
            skLineSegment(sketch, "E578", {"start": v(-32.7, 9.75) * mm, "end": v(-32.48, 9.8) * mm});
            skLineSegment(sketch, "E579", {"start": v(-32.48, 9.8) * mm, "end": v(-32.25, 9.8) * mm});
            skLineSegment(sketch, "E580", {"start": v(-32.25, 9.8) * mm, "end": v(-32.02, 9.8) * mm});
            skLineSegment(sketch, "E581", {"start": v(-32.02, 9.8) * mm, "end": v(-31.8, 9.8) * mm});
            skLineSegment(sketch, "E582", {"start": v(-31.8, 9.8) * mm, "end": v(-31.57, 9.75) * mm});
            skLineSegment(sketch, "E583", {"start": v(-31.57, 9.75) * mm, "end": v(-31.37, 9.7) * mm});
            skLineSegment(sketch, "E584", {"start": v(-31.37, 9.7) * mm, "end": v(-31.17, 9.62) * mm});
            skLineSegment(sketch, "E585", {"start": v(-31.17, 9.62) * mm, "end": v(-30.98, 9.52) * mm});
            skLineSegment(sketch, "E586", {"start": v(-30.98, 9.52) * mm, "end": v(-30.8, 9.4) * mm});
            skLineSegment(sketch, "E587", {"start": v(-30.8, 9.4) * mm, "end": v(-30.64, 9.28) * mm});
            skLineSegment(sketch, "E588", {"start": v(-30.64, 9.28) * mm, "end": v(-30.48, 9.12) * mm});
            skLineSegment(sketch, "E589", {"start": v(-30.48, 9.12) * mm, "end": v(-30.34, 8.96) * mm});
            skLineSegment(sketch, "E590", {"start": v(-30.34, 8.96) * mm, "end": v(-30.22, 8.79) * mm});
            skLineSegment(sketch, "E591", {"start": v(-30.22, 8.79) * mm, "end": v(-30.12, 8.6) * mm});
            skLineSegment(sketch, "E592", {"start": v(-30.12, 8.6) * mm, "end": v(-30.04, 8.4) * mm});
            skLineSegment(sketch, "E593", {"start": v(-30.04, 8.4) * mm, "end": v(-29.97, 8.2) * mm});
            skLineSegment(sketch, "E594", {"start": v(-29.97, 8.2) * mm, "end": v(-29.93, 8) * mm});
            skLineSegment(sketch, "E595", {"start": v(-29.93, 8) * mm, "end": v(-29.9, 7.77) * mm});
            skLineSegment(sketch, "E596", {"start": v(-29.9, 7.77) * mm, "end": v(-29.9, 7.54) * mm});
            skLineSegment(sketch, "E597", {"start": v(-29.9, 7.54) * mm, "end": v(-29.91, 7.3) * mm});
            skLineSegment(sketch, "E598", {"start": v(-29.91, 7.3) * mm, "end": v(-29.95, 7.1) * mm});
            skLineSegment(sketch, "E599", {"start": v(-29.95, 7.1) * mm, "end": v(-30, 6.88) * mm});
            skLineSegment(sketch, "E600", {"start": v(-30, 6.88) * mm, "end": v(-30.07, 6.69) * mm});
            skLineSegment(sketch, "E601", {"start": v(-30.07, 6.69) * mm, "end": v(-30.16, 6.5) * mm});
            skLineSegment(sketch, "E602", {"start": v(-30.16, 6.5) * mm, "end": v(-30.27, 6.32) * mm});
            skLineSegment(sketch, "E603", {"start": v(-30.27, 6.32) * mm, "end": v(-30.4, 6.16) * mm});
            skLineSegment(sketch, "E604", {"start": v(-30.4, 6.16) * mm, "end": v(-30.55, 6) * mm});
            skLineSegment(sketch, "E605", {"start": v(-30.55, 6) * mm, "end": v(-30.71, 5.86) * mm});
            skLineSegment(sketch, "E606", {"start": v(-30.71, 5.86) * mm, "end": v(-30.89, 5.74) * mm});
            skLineSegment(sketch, "E607", {"start": v(-30.89, 5.74) * mm, "end": v(-31.07, 5.64) * mm});
            skLineSegment(sketch, "E608", {"start": v(-31.07, 5.64) * mm, "end": v(-31.26, 5.55) * mm});
            skLineSegment(sketch, "E609", {"start": v(-31.26, 5.55) * mm, "end": v(-31.47, 5.49) * mm});
            skLineSegment(sketch, "E610", {"start": v(-31.47, 5.49) * mm, "end": v(-31.68, 5.44) * mm});
            skLineSegment(sketch, "E611", {"start": v(-31.68, 5.44) * mm, "end": v(-31.9, 5.41) * mm});
            skLineSegment(sketch, "E612", {"start": v(-31.9, 5.41) * mm, "end": v(-32.14, 5.4) * mm});
            skLineSegment(sketch, "E613", {"start": v(-33.5, 7.6) * mm, "end": v(-33.5, 7.48) * mm});
            skLineSegment(sketch, "E614", {"start": v(-33.5, 7.48) * mm, "end": v(-33.48, 7.35) * mm});
            skLineSegment(sketch, "E615", {"start": v(-33.48, 7.35) * mm, "end": v(-33.46, 7.23) * mm});
            skLineSegment(sketch, "E616", {"start": v(-33.46, 7.23) * mm, "end": v(-33.42, 7.12) * mm});
            skLineSegment(sketch, "E617", {"start": v(-33.42, 7.12) * mm, "end": v(-33.36, 7.01) * mm});
            skLineSegment(sketch, "E618", {"start": v(-33.36, 7.01) * mm, "end": v(-33.3, 6.91) * mm});
            skLineSegment(sketch, "E619", {"start": v(-33.3, 6.91) * mm, "end": v(-33.22, 6.82) * mm});
            skLineSegment(sketch, "E620", {"start": v(-33.22, 6.82) * mm, "end": v(-33.13, 6.73) * mm});
            skLineSegment(sketch, "E621", {"start": v(-33.13, 6.73) * mm, "end": v(-33.04, 6.65) * mm});
            skLineSegment(sketch, "E622", {"start": v(-33.04, 6.65) * mm, "end": v(-32.93, 6.59) * mm});
            skLineSegment(sketch, "E623", {"start": v(-32.93, 6.59) * mm, "end": v(-32.82, 6.53) * mm});
            skLineSegment(sketch, "E624", {"start": v(-32.82, 6.53) * mm, "end": v(-32.7, 6.48) * mm});
            skLineSegment(sketch, "E625", {"start": v(-32.7, 6.48) * mm, "end": v(-32.57, 6.44) * mm});
            skLineSegment(sketch, "E626", {"start": v(-32.57, 6.44) * mm, "end": v(-32.44, 6.41) * mm});
            skLineSegment(sketch, "E627", {"start": v(-32.44, 6.41) * mm, "end": v(-32.3, 6.4) * mm});
            skLineSegment(sketch, "E628", {"start": v(-32.3, 6.4) * mm, "end": v(-32.15, 6.39) * mm});
            skLineSegment(sketch, "E629", {"start": v(-32.15, 6.39) * mm, "end": v(-32.01, 6.39) * mm});
            skLineSegment(sketch, "E630", {"start": v(-32.01, 6.39) * mm, "end": v(-31.87, 6.4) * mm});
            skLineSegment(sketch, "E631", {"start": v(-31.87, 6.4) * mm, "end": v(-31.74, 6.43) * mm});
            skLineSegment(sketch, "E632", {"start": v(-31.74, 6.43) * mm, "end": v(-31.62, 6.46) * mm});
            skLineSegment(sketch, "E633", {"start": v(-31.62, 6.46) * mm, "end": v(-31.5, 6.5) * mm});
            skLineSegment(sketch, "E634", {"start": v(-31.5, 6.5) * mm, "end": v(-31.4, 6.56) * mm});
            skLineSegment(sketch, "E635", {"start": v(-31.4, 6.56) * mm, "end": v(-31.29, 6.62) * mm});
            skLineSegment(sketch, "E636", {"start": v(-31.29, 6.62) * mm, "end": v(-31.19, 6.7) * mm});
            skLineSegment(sketch, "E637", {"start": v(-31.19, 6.7) * mm, "end": v(-31.1, 6.78) * mm});
            skLineSegment(sketch, "E638", {"start": v(-31.1, 6.78) * mm, "end": v(-31.01, 6.87) * mm});
            skLineSegment(sketch, "E639", {"start": v(-31.01, 6.87) * mm, "end": v(-30.94, 6.97) * mm});
            skLineSegment(sketch, "E640", {"start": v(-30.94, 6.97) * mm, "end": v(-30.88, 7.07) * mm});
            skLineSegment(sketch, "E641", {"start": v(-30.88, 7.07) * mm, "end": v(-30.84, 7.18) * mm});
            skLineSegment(sketch, "E642", {"start": v(-30.84, 7.18) * mm, "end": v(-30.8, 7.3) * mm});
            skLineSegment(sketch, "E643", {"start": v(-30.8, 7.3) * mm, "end": v(-30.78, 7.4) * mm});
            skLineSegment(sketch, "E644", {"start": v(-30.78, 7.4) * mm, "end": v(-30.77, 7.53) * mm});
            skLineSegment(sketch, "E645", {"start": v(-30.77, 7.53) * mm, "end": v(-30.77, 7.66) * mm});
            skLineSegment(sketch, "E646", {"start": v(-30.77, 7.66) * mm, "end": v(-30.78, 7.8) * mm});
            skLineSegment(sketch, "E647", {"start": v(-30.78, 7.8) * mm, "end": v(-30.8, 7.91) * mm});
            skLineSegment(sketch, "E648", {"start": v(-30.8, 7.91) * mm, "end": v(-30.84, 8.03) * mm});
            skLineSegment(sketch, "E649", {"start": v(-30.84, 8.03) * mm, "end": v(-30.88, 8.14) * mm});
            skLineSegment(sketch, "E650", {"start": v(-30.88, 8.14) * mm, "end": v(-30.94, 8.24) * mm});
            skLineSegment(sketch, "E651", {"start": v(-30.94, 8.24) * mm, "end": v(-31, 8.34) * mm});
            skLineSegment(sketch, "E652", {"start": v(-31, 8.34) * mm, "end": v(-31.09, 8.43) * mm});
            skLineSegment(sketch, "E653", {"start": v(-31.09, 8.43) * mm, "end": v(-31.18, 8.51) * mm});
            skLineSegment(sketch, "E654", {"start": v(-31.18, 8.51) * mm, "end": v(-31.28, 8.59) * mm});
            skLineSegment(sketch, "E655", {"start": v(-31.28, 8.59) * mm, "end": v(-31.39, 8.65) * mm});
            skLineSegment(sketch, "E656", {"start": v(-31.39, 8.65) * mm, "end": v(-31.5, 8.7) * mm});
            skLineSegment(sketch, "E657", {"start": v(-31.5, 8.7) * mm, "end": v(-31.62, 8.75) * mm});
            skLineSegment(sketch, "E658", {"start": v(-31.62, 8.75) * mm, "end": v(-31.75, 8.78) * mm});
            skLineSegment(sketch, "E659", {"start": v(-31.75, 8.78) * mm, "end": v(-31.89, 8.8) * mm});
            skLineSegment(sketch, "E660", {"start": v(-31.89, 8.8) * mm, "end": v(-32.03, 8.82) * mm});
            skLineSegment(sketch, "E661", {"start": v(-32.03, 8.82) * mm, "end": v(-32.18, 8.82) * mm});
            skLineSegment(sketch, "E662", {"start": v(-32.18, 8.82) * mm, "end": v(-32.32, 8.81) * mm});
            skLineSegment(sketch, "E663", {"start": v(-32.32, 8.81) * mm, "end": v(-32.46, 8.8) * mm});
            skLineSegment(sketch, "E664", {"start": v(-32.46, 8.8) * mm, "end": v(-32.6, 8.77) * mm});
            skLineSegment(sketch, "E665", {"start": v(-32.6, 8.77) * mm, "end": v(-32.72, 8.73) * mm});
            skLineSegment(sketch, "E666", {"start": v(-32.72, 8.73) * mm, "end": v(-32.83, 8.68) * mm});
            skLineSegment(sketch, "E667", {"start": v(-32.83, 8.68) * mm, "end": v(-32.94, 8.63) * mm});
            skLineSegment(sketch, "E668", {"start": v(-32.94, 8.63) * mm, "end": v(-33.04, 8.56) * mm});
            skLineSegment(sketch, "E669", {"start": v(-33.04, 8.56) * mm, "end": v(-33.13, 8.48) * mm});
            skLineSegment(sketch, "E670", {"start": v(-33.13, 8.48) * mm, "end": v(-33.22, 8.4) * mm});
            skLineSegment(sketch, "E671", {"start": v(-33.22, 8.4) * mm, "end": v(-33.3, 8.3) * mm});
            skLineSegment(sketch, "E672", {"start": v(-33.3, 8.3) * mm, "end": v(-33.35, 8.2) * mm});
            skLineSegment(sketch, "E673", {"start": v(-33.35, 8.2) * mm, "end": v(-33.4, 8.1) * mm});
            skLineSegment(sketch, "E674", {"start": v(-33.4, 8.1) * mm, "end": v(-33.45, 7.99) * mm});
            skLineSegment(sketch, "E675", {"start": v(-33.45, 7.99) * mm, "end": v(-33.48, 7.87) * mm});
            skLineSegment(sketch, "E676", {"start": v(-33.48, 7.87) * mm, "end": v(-33.5, 7.74) * mm});
            skLineSegment(sketch, "E677", {"start": v(-33.5, 7.74) * mm, "end": v(-33.5, 7.6) * mm});
            skLineSegment(sketch, "E678", {"start": v(-34.33, 13.8) * mm, "end": v(-34.33, 13.83) * mm});
            skLineSegment(sketch, "E679", {"start": v(-34.33, 13.83) * mm, "end": v(-34.33, 13.9) * mm});
            skLineSegment(sketch, "E680", {"start": v(-34.33, 13.9) * mm, "end": v(-34.33, 13.97) * mm});
            skLineSegment(sketch, "E681", {"start": v(-34.33, 13.97) * mm, "end": v(-34.33, 14.05) * mm});
            skLineSegment(sketch, "E682", {"start": v(-34.33, 14.05) * mm, "end": v(-34.33, 14.1) * mm});
            skLineSegment(sketch, "E683", {"start": v(-34.33, 14.1) * mm, "end": v(-34.33, 14.15) * mm});
            skLineSegment(sketch, "E684", {"start": v(-34.33, 14.15) * mm, "end": v(-34.3, 14.23) * mm});
            skLineSegment(sketch, "E685", {"start": v(-34.3, 14.23) * mm, "end": v(-34.26, 14.3) * mm});
            skLineSegment(sketch, "E686", {"start": v(-34.26, 14.3) * mm, "end": v(-34.2, 14.36) * mm});
            skLineSegment(sketch, "E687", {"start": v(-34.2, 14.36) * mm, "end": v(-34.12, 14.4) * mm});
            skLineSegment(sketch, "E688", {"start": v(-34.12, 14.4) * mm, "end": v(-34.03, 14.41) * mm});
            skLineSegment(sketch, "E689", {"start": v(-34.03, 14.41) * mm, "end": v(-33.76, 14.41) * mm});
            skLineSegment(sketch, "E690", {"start": v(-33.76, 14.41) * mm, "end": v(-33.01, 14.41) * mm});
            skLineSegment(sketch, "E691", {"start": v(-33.01, 14.41) * mm, "end": v(-32.03, 14.41) * mm});
            skLineSegment(sketch, "E692", {"start": v(-32.03, 14.41) * mm, "end": v(-31.07, 14.41) * mm});
            skLineSegment(sketch, "E693", {"start": v(-31.07, 14.41) * mm, "end": v(-30.41, 14.41) * mm});
            skLineSegment(sketch, "E694", {"start": v(-30.41, 14.41) * mm, "end": v(-30.23, 14.41) * mm});
            skLineSegment(sketch, "E695", {"start": v(-30.23, 14.41) * mm, "end": v(-30.15, 14.4) * mm});
            skLineSegment(sketch, "E696", {"start": v(-30.15, 14.4) * mm, "end": v(-30.07, 14.35) * mm});
            skLineSegment(sketch, "E697", {"start": v(-30.07, 14.35) * mm, "end": v(-30.01, 14.29) * mm});
            skLineSegment(sketch, "E698", {"start": v(-30.01, 14.29) * mm, "end": v(-29.97, 14.21) * mm});
            skLineSegment(sketch, "E699", {"start": v(-29.97, 14.21) * mm, "end": v(-29.95, 14.13) * mm});
            skLineSegment(sketch, "E700", {"start": v(-29.95, 14.13) * mm, "end": v(-29.95, 14.08) * mm});
            skLineSegment(sketch, "E701", {"start": v(-29.95, 14.08) * mm, "end": v(-29.95, 14) * mm});
            skLineSegment(sketch, "E702", {"start": v(-29.95, 14) * mm, "end": v(-29.95, 13.88) * mm});
            skLineSegment(sketch, "E703", {"start": v(-29.95, 13.88) * mm, "end": v(-29.95, 13.76) * mm});
            skLineSegment(sketch, "E704", {"start": v(-29.95, 13.76) * mm, "end": v(-29.95, 13.68) * mm});
            skLineSegment(sketch, "E705", {"start": v(-29.95, 13.68) * mm, "end": v(-29.95, 13.64) * mm});
            skLineSegment(sketch, "E706", {"start": v(-29.95, 13.64) * mm, "end": v(-29.96, 13.6) * mm});
            skLineSegment(sketch, "E707", {"start": v(-29.96, 13.6) * mm, "end": v(-29.98, 13.54) * mm});
            skLineSegment(sketch, "E708", {"start": v(-29.98, 13.54) * mm, "end": v(-30, 13.5) * mm});
            skLineSegment(sketch, "E709", {"start": v(-30, 13.5) * mm, "end": v(-30.03, 13.45) * mm});
            skLineSegment(sketch, "E710", {"start": v(-30.03, 13.45) * mm, "end": v(-30.07, 13.41) * mm});
            skLineSegment(sketch, "E711", {"start": v(-30.07, 13.41) * mm, "end": v(-30.2, 13.33) * mm});
            skLineSegment(sketch, "E712", {"start": v(-30.2, 13.33) * mm, "end": v(-30.67, 13) * mm});
            skLineSegment(sketch, "E713", {"start": v(-30.67, 13) * mm, "end": v(-31.35, 12.5) * mm});
            skLineSegment(sketch, "E714", {"start": v(-31.35, 12.5) * mm, "end": v(-32.06, 12) * mm});
            skLineSegment(sketch, "E715", {"start": v(-32.06, 12) * mm, "end": v(-32.6, 11.63) * mm});
            skLineSegment(sketch, "E716", {"start": v(-32.6, 11.63) * mm, "end": v(-32.78, 11.5) * mm});
            skLineSegment(sketch, "E717", {"start": v(-32.78, 11.5) * mm, "end": v(-32.52, 11.5) * mm});
            skLineSegment(sketch, "E718", {"start": v(-32.52, 11.5) * mm, "end": v(-31.97, 11.5) * mm});
            skLineSegment(sketch, "E719", {"start": v(-31.97, 11.5) * mm, "end": v(-31.3, 11.5) * mm});
            skLineSegment(sketch, "E720", {"start": v(-31.3, 11.5) * mm, "end": v(-30.69, 11.5) * mm});
            skLineSegment(sketch, "E721", {"start": v(-30.69, 11.5) * mm, "end": v(-30.3, 11.5) * mm});
            skLineSegment(sketch, "E722", {"start": v(-30.3, 11.5) * mm, "end": v(-30.21, 11.5) * mm});
            skLineSegment(sketch, "E723", {"start": v(-30.21, 11.5) * mm, "end": v(-30.13, 11.47) * mm});
            skLineSegment(sketch, "E724", {"start": v(-30.13, 11.47) * mm, "end": v(-30.06, 11.42) * mm});
            skLineSegment(sketch, "E725", {"start": v(-30.06, 11.42) * mm, "end": v(-30, 11.35) * mm});
            skLineSegment(sketch, "E726", {"start": v(-30, 11.35) * mm, "end": v(-29.97, 11.27) * mm});
            skLineSegment(sketch, "E727", {"start": v(-29.97, 11.27) * mm, "end": v(-29.95, 11.19) * mm});
            skLineSegment(sketch, "E728", {"start": v(-29.95, 11.19) * mm, "end": v(-29.95, 11.16) * mm});
            skLineSegment(sketch, "E729", {"start": v(-29.95, 11.16) * mm, "end": v(-29.95, 11.1) * mm});
            skLineSegment(sketch, "E730", {"start": v(-29.95, 11.1) * mm, "end": v(-29.95, 11) * mm});
            skLineSegment(sketch, "E731", {"start": v(-29.95, 11) * mm, "end": v(-29.95, 10.92) * mm});
            skLineSegment(sketch, "E732", {"start": v(-29.95, 10.92) * mm, "end": v(-29.95, 10.87) * mm});
            skLineSegment(sketch, "E733", {"start": v(-29.95, 10.87) * mm, "end": v(-29.96, 10.82) * mm});
            skLineSegment(sketch, "E734", {"start": v(-29.96, 10.82) * mm, "end": v(-29.98, 10.74) * mm});
            skLineSegment(sketch, "E735", {"start": v(-29.98, 10.74) * mm, "end": v(-30.02, 10.66) * mm});
            skLineSegment(sketch, "E736", {"start": v(-30.02, 10.66) * mm, "end": v(-30.09, 10.6) * mm});
            skLineSegment(sketch, "E737", {"start": v(-30.09, 10.6) * mm, "end": v(-30.16, 10.57) * mm});
            skLineSegment(sketch, "E738", {"start": v(-30.16, 10.57) * mm, "end": v(-30.25, 10.55) * mm});
            skLineSegment(sketch, "E739", {"start": v(-30.25, 10.55) * mm, "end": v(-30.52, 10.55) * mm});
            skLineSegment(sketch, "E740", {"start": v(-30.52, 10.55) * mm, "end": v(-31.27, 10.55) * mm});
            skLineSegment(sketch, "E741", {"start": v(-31.27, 10.55) * mm, "end": v(-32.25, 10.55) * mm});
            skLineSegment(sketch, "E742", {"start": v(-32.25, 10.55) * mm, "end": v(-33.2, 10.55) * mm});
            skLineSegment(sketch, "E743", {"start": v(-33.2, 10.55) * mm, "end": v(-33.87, 10.55) * mm});
            skLineSegment(sketch, "E744", {"start": v(-33.87, 10.55) * mm, "end": v(-34.05, 10.55) * mm});
            skLineSegment(sketch, "E745", {"start": v(-34.05, 10.55) * mm, "end": v(-34.14, 10.57) * mm});
            skLineSegment(sketch, "E746", {"start": v(-34.14, 10.57) * mm, "end": v(-34.21, 10.62) * mm});
            skLineSegment(sketch, "E747", {"start": v(-34.21, 10.62) * mm, "end": v(-34.27, 10.68) * mm});
            skLineSegment(sketch, "E748", {"start": v(-34.27, 10.68) * mm, "end": v(-34.31, 10.75) * mm});
            skLineSegment(sketch, "E749", {"start": v(-34.31, 10.75) * mm, "end": v(-34.33, 10.84) * mm});
            skLineSegment(sketch, "E750", {"start": v(-34.33, 10.84) * mm, "end": v(-34.33, 10.89) * mm});
            skLineSegment(sketch, "E751", {"start": v(-34.33, 10.89) * mm, "end": v(-34.33, 10.97) * mm});
            skLineSegment(sketch, "E752", {"start": v(-34.33, 10.97) * mm, "end": v(-34.33, 11.1) * mm});
            skLineSegment(sketch, "E753", {"start": v(-34.33, 11.1) * mm, "end": v(-34.33, 11.21) * mm});
            skLineSegment(sketch, "E754", {"start": v(-34.33, 11.21) * mm, "end": v(-34.33, 11.3) * mm});
            skLineSegment(sketch, "E755", {"start": v(-34.33, 11.3) * mm, "end": v(-34.33, 11.34) * mm});
            skLineSegment(sketch, "E756", {"start": v(-34.33, 11.34) * mm, "end": v(-34.32, 11.4) * mm});
            skLineSegment(sketch, "E757", {"start": v(-34.32, 11.4) * mm, "end": v(-34.3, 11.44) * mm});
            skLineSegment(sketch, "E758", {"start": v(-34.3, 11.44) * mm, "end": v(-34.28, 11.49) * mm});
            skLineSegment(sketch, "E759", {"start": v(-34.28, 11.49) * mm, "end": v(-34.25, 11.53) * mm});
            skLineSegment(sketch, "E760", {"start": v(-34.25, 11.53) * mm, "end": v(-34.21, 11.57) * mm});
            skLineSegment(sketch, "E761", {"start": v(-34.21, 11.57) * mm, "end": v(-34.1, 11.65) * mm});
            skLineSegment(sketch, "E762", {"start": v(-34.1, 11.65) * mm, "end": v(-33.62, 12) * mm});
            skLineSegment(sketch, "E763", {"start": v(-33.62, 12) * mm, "end": v(-32.94, 12.48) * mm});
            skLineSegment(sketch, "E764", {"start": v(-32.94, 12.48) * mm, "end": v(-32.24, 12.98) * mm});
            skLineSegment(sketch, "E765", {"start": v(-32.24, 12.98) * mm, "end": v(-31.7, 13.36) * mm});
            skLineSegment(sketch, "E766", {"start": v(-31.7, 13.36) * mm, "end": v(-31.52, 13.5) * mm});
            skLineSegment(sketch, "E767", {"start": v(-31.52, 13.5) * mm, "end": v(-31.78, 13.5) * mm});
            skLineSegment(sketch, "E768", {"start": v(-31.78, 13.5) * mm, "end": v(-32.33, 13.5) * mm});
            skLineSegment(sketch, "E769", {"start": v(-32.33, 13.5) * mm, "end": v(-33, 13.5) * mm});
            skLineSegment(sketch, "E770", {"start": v(-33, 13.5) * mm, "end": v(-33.6, 13.5) * mm});
            skLineSegment(sketch, "E771", {"start": v(-33.6, 13.5) * mm, "end": v(-33.97, 13.5) * mm});
            skLineSegment(sketch, "E772", {"start": v(-33.97, 13.5) * mm, "end": v(-34.07, 13.5) * mm});
            skLineSegment(sketch, "E773", {"start": v(-34.07, 13.5) * mm, "end": v(-34.15, 13.52) * mm});
            skLineSegment(sketch, "E774", {"start": v(-34.15, 13.52) * mm, "end": v(-34.22, 13.57) * mm});
            skLineSegment(sketch, "E775", {"start": v(-34.22, 13.57) * mm, "end": v(-34.28, 13.63) * mm});
            skLineSegment(sketch, "E776", {"start": v(-34.28, 13.63) * mm, "end": v(-34.32, 13.71) * mm});
            skLineSegment(sketch, "E777", {"start": v(-34.32, 13.71) * mm, "end": v(-34.33, 13.8) * mm});
            skSolve(sketch);
        }
        {
            var Q0;
            Q0=makeQuery(id+"F13.imprint","IMPRINT",FACE,{"disambiguationData":[TD([[makeQuery(id+"F13.imprint","IMPRINT",EDGE,{"derivedFrom":sQuery(id+"F13.wireOp",EDGE,"E678")}),-1.0]])]});
            var Q1;
            Q1=makeQuery(id+"F13.imprint","IMPRINT",FACE,{"disambiguationData":[TD([[makeQuery(id+"F13.imprint","IMPRINT",EDGE,{"derivedFrom":sQuery(id+"F13.wireOp",EDGE,"E548")}),-1.0]])]});
            var Q2;
            Q2=makeQuery(id+"F13.imprint","IMPRINT",FACE,{"disambiguationData":[TD([[makeQuery(id+"F13.imprint","IMPRINT",EDGE,{"derivedFrom":sQuery(id+"F13.wireOp",EDGE,"E405")}),-1.0]])]});
            var Q3;
            Q3=makeQuery(id+"F13.imprint","IMPRINT",FACE,{"disambiguationData":[TD([[makeQuery(id+"F13.imprint","IMPRINT",EDGE,{"derivedFrom":sQuery(id+"F13.wireOp",EDGE,"E306")}),-1.0]])]});
            var Q4;
            Q4=makeQuery(id+"F13.imprint","IMPRINT",FACE,{"disambiguationData":[TD([[makeQuery(id+"F13.imprint","IMPRINT",EDGE,{"derivedFrom":sQuery(id+"F13.wireOp",EDGE,"E206")}),-1.0]])]});
            var Q5;
            Q5=makeQuery(id+"F13.imprint","IMPRINT",FACE,{"disambiguationData":[TD([[makeQuery(id+"F13.imprint","IMPRINT",EDGE,{"derivedFrom":sQuery(id+"F13.wireOp",EDGE,"E106")}),-1.0]])]});
            var Q6;
            Q6=makeQuery(id+"F13.imprint","IMPRINT",FACE,{"disambiguationData":[TD([[makeQuery(id+"F13.imprint","IMPRINT",EDGE,{"derivedFrom":sQuery(id+"F13.wireOp",EDGE,"E6")}),-1.0]])]});
            extrude(context, id + "F14", {"entities" : qUnion([Q0, Q1, Q2, Q3, Q4, Q5, Q6]), "operationType" : NewBodyOperationType.REMOVE, "oppositeDirection" : true, "depth" : 1 * mm});
        }
    });
